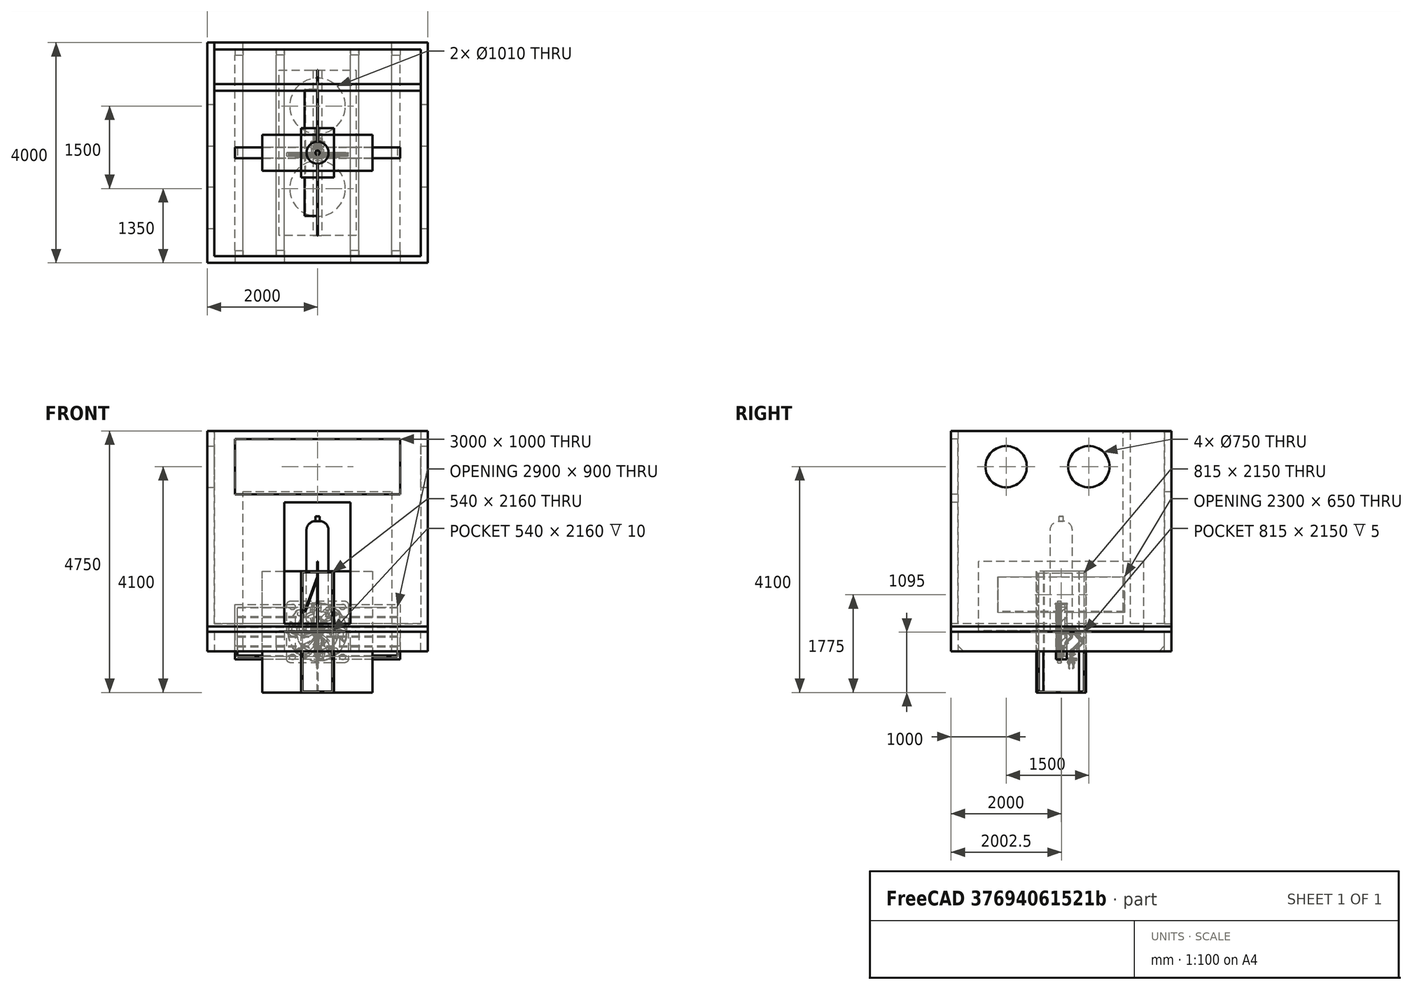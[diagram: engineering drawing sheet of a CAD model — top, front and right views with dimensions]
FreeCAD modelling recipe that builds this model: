
FCSTD DOCUMENT  (FreeCAD 0.19R22989 (Git))
Label: OCPMDC4_v2_asm
License: All rights reserved
LicenseURL: http://en.wikipedia.org/wiki/All_rights_reserved
objects: Part::Feature×54, App::Link×34, Sketcher::SketchObject×24, App::Part×19, TechDraw::DrawViewDimension×17, PartDesign::Pad×16, PartDesign::CoordinateSystem×13, PartDesign::Body×9, PartDesign::Pocket×6, TechDraw::DrawViewPart×6, Part::FeaturePython×3, App::MeasureDistance×3, TechDraw::DrawSVGTemplate×2, TechDraw::DrawPage×2, App::DocumentObjectGroup×2, PartDesign::Mirrored×2, PartDesign::Revolution×2, PartDesign::Chamfer×1, App::FeaturePython×1
note: 155 computed .brp shape members not serialized (recipe doc carries the construction recipe); baked Part::Feature solids carry a one-line shape summary decoded from their .brp

FEATURE [Sketcher::SketchObject] Sketch
  MapMode = 5
  Support = -> [XY_Plane]
  sketch-geometry (4):
    g0: LineSegment StartX=-1875 StartY=1875 StartZ=0 EndX=1875 EndY=1875 EndZ=0
    g1: LineSegment StartX=1875 StartY=1875 StartZ=0 EndX=1875 EndY=-1875 EndZ=0
    g2: LineSegment StartX=1875 StartY=-1875 StartZ=0 EndX=-1875 EndY=-1875 EndZ=0
    g3: LineSegment StartX=-1875 StartY=-1875 StartZ=0 EndX=-1875 EndY=1875 EndZ=0
  constraints (10):
    c: Coincident(g0,g1)
    c: Coincident(g1,g2)
    c: Coincident(g2,g3)
    c: Coincident(g3,g0)
    c: Horizontal(g2)
    c: Vertical(g3)
    c: DistanceX(g0,g0) = 3750
    c: DistanceY(g1,g1) = 3750
    c: Symmetric(g0,g0,g-2)
    c: Symmetric(g0,g1,g-1)
FEATURE [PartDesign::Pad] Pad
  Direction = (1,1,1)
  Length = 150
  Length2 = 100
  Profile = -> Sketch
  Type = 0
FEATURE [Sketcher::SketchObject] Sketch001
  ExternalGeometry = -> [Pad]
  MapMode = 5
  Placement = pos=(0,-1875,0) rot=(1,0,0;1.5708rad)
  Support = -> [Pad]
  sketch-geometry (16):
    g0: LineSegment StartX=-1350 StartY=0 StartZ=0 EndX=-1500 EndY=0 EndZ=0
    g1: LineSegment StartX=-1500 StartY=0 StartZ=0 EndX=-1500 EndY=-350 EndZ=0
    g2: LineSegment StartX=-1500 StartY=-350 StartZ=0 EndX=-1350 EndY=-350 EndZ=0
    g3: LineSegment StartX=-1350 StartY=-350 StartZ=0 EndX=-1350 EndY=0 EndZ=0
    g4: LineSegment StartX=-750 StartY=0 StartZ=0 EndX=-600 EndY=0 EndZ=0
    g5: LineSegment StartX=-600 StartY=0 StartZ=0 EndX=-600 EndY=-350 EndZ=0
    g6: LineSegment StartX=-600 StartY=-350 StartZ=0 EndX=-750 EndY=-350 EndZ=0
    g7: LineSegment StartX=-750 StartY=-350 StartZ=0 EndX=-750 EndY=0 EndZ=0
    g8: LineSegment StartX=600 StartY=0 StartZ=0 EndX=750 EndY=0 EndZ=0
    g9: LineSegment StartX=750 StartY=0 StartZ=0 EndX=750 EndY=-350 EndZ=0
    g10: LineSegment StartX=750 StartY=-350 StartZ=0 EndX=600 EndY=-350 EndZ=0
    g11: LineSegment StartX=600 StartY=-350 StartZ=0 EndX=600 EndY=0 EndZ=0
    g12: LineSegment StartX=1500 StartY=0 StartZ=0 EndX=1350 EndY=0 EndZ=0
    g13: LineSegment StartX=1350 StartY=0 StartZ=0 EndX=1350 EndY=-350 EndZ=0
    g14: LineSegment StartX=1350 StartY=-350 StartZ=0 EndX=1500 EndY=-350 EndZ=0
    g15: LineSegment StartX=1500 StartY=-350 StartZ=0 EndX=1500 EndY=0 EndZ=0
  constraints (48):
    c: Coincident(g0,g1)
    c: Coincident(g1,g2)
    c: Coincident(g2,g3)
    c: Coincident(g3,g0)
    c: Horizontal(g0)
    c: Horizontal(g2)
    c: Vertical(g1)
    c: Vertical(g3)
    c: PointOnObject(g0,g-1)
    c: DistanceX(g0,g0) = 150
    c: DistanceY(g2,g-1) = 350
    c: Coincident(g4,g5)
    c: Coincident(g5,g6)
    c: Coincident(g6,g7)
    c: Coincident(g7,g4)
    c: Horizontal(g4)
    c: Horizontal(g6)
    c: Vertical(g5)
    c: Vertical(g7)
    c: PointOnObject(g4,g-1)
    c: Coincident(g8,g9)
    c: Coincident(g9,g10)
    c: Coincident(g10,g11)
    c: Coincident(g11,g8)
    c: Horizontal(g8)
    c: Horizontal(g10)
    c: Vertical(g9)
    c: Vertical(g11)
    c: PointOnObject(g8,g-1)
    c: Coincident(g12,g13)
    c: Coincident(g13,g14)
    c: Coincident(g14,g15)
    c: Coincident(g15,g12)
    c: Horizontal(g12)
    c: Horizontal(g14)
    c: Vertical(g13)
    c: Vertical(g15)
    c: PointOnObject(g12,g-1)
    c: Horizontal(g6,g1)
    c: Horizontal(g1,g10)
    c: Horizontal(g10,g13)
    c: DistanceX(g4,g4) = 150
    c: DistanceX(g-3,g4) = 1275
    c: DistanceX(g-3,g0) = 375
    c: DistanceX(g12,g-4) = 375
    c: DistanceX(g12,g12) = 150
    c: DistanceX(g8,g-4) = 1275
    c: DistanceX(g8,g8) = 150
FEATURE [PartDesign::Pad] Pad001
  BaseFeature = -> Pad
  Direction = (1,1,1)
  Length = 3750
  Length2 = 100
  Profile = -> Sketch001
  Reversed = true
  Type = 0
FEATURE [PartDesign::Chamfer] Chamfer
  Angle = 45
  Base = -> Pad001 [Edge52,Edge58,Edge63,Edge67,Edge40,Edge34,Edge28,Edge22]
  BaseFeature = -> Pad001
  ChamferType = 0
  FlipDirection = false
  Size = 100
  Size2 = 1
  SupportTransform = false
FEATURE [Sketcher::SketchObject] Sketch002
  ExternalGeometry = -> [Chamfer]
  MapMode = 5
  Placement = pos=(-1875,0,0) rot=(0.57735,-0.57735,-0.57735;2.0944rad)
  Support = -> [Chamfer]
  sketch-geometry (4):
    g0: LineSegment StartX=-2000 StartY=-350 StartZ=0 EndX=2000 EndY=-350 EndZ=0
    g1: LineSegment StartX=2000 StartY=-350 StartZ=0 EndX=2000 EndY=3650 EndZ=0
    g2: LineSegment StartX=2000 StartY=3650 StartZ=0 EndX=-2000 EndY=3650 EndZ=0
    g3: LineSegment StartX=-2000 StartY=3650 StartZ=0 EndX=-2000 EndY=-350 EndZ=0
  constraints (12):
    c: Coincident(g0,g1)
    c: Coincident(g1,g2)
    c: Coincident(g2,g3)
    c: Coincident(g3,g0)
    c: Horizontal(g0)
    c: Horizontal(g2)
    c: Vertical(g1)
    c: Vertical(g3)
    c: DistanceX(g2,g2) = 4000
    c: DistanceY(g1,g1) = 4000
    c: DistanceX(g-1,g0) = 2000
    c: Horizontal(g0,g-5)
FEATURE [PartDesign::Pad] Pad002
  BaseFeature = -> Chamfer
  Direction = (1,1,1)
  Length = 125
  Length2 = 100
  Profile = -> Sketch002
  Type = 0
FEATURE [Sketcher::SketchObject] Sketch003
  ExternalGeometry = -> [Pad002]
  MapMode = 5
  Placement = pos=(1875,0,0) rot=(0.57735,0.57735,0.57735;2.0944rad)
  Support = -> [Pad002]
  sketch-geometry (4):
    g0: LineSegment StartX=1250 StartY=150 StartZ=0 EndX=1125 EndY=150 EndZ=0
    g1: LineSegment StartX=1125 StartY=150 StartZ=0 EndX=1125 EndY=3637.44 EndZ=0
    g2: LineSegment StartX=1125 StartY=3637.44 StartZ=0 EndX=1250 EndY=3637.44 EndZ=0
    g3: LineSegment StartX=1250 StartY=3637.44 StartZ=0 EndX=1250 EndY=150 EndZ=0
  constraints (12):
    c: Coincident(g0,g1)
    c: Coincident(g1,g2)
    c: Coincident(g2,g3)
    c: Coincident(g3,g0)
    c: Horizontal(g0)
    c: Horizontal(g2)
    c: Vertical(g1)
    c: Vertical(g3)
    c: PointOnObject(g0,g-7)
    c: DistanceX(g2,g2) = 125
    c: DistanceX(g-7,g1) = 3000
    c: DistanceY(g3,g3) = 3487.44
FEATURE [PartDesign::Pad] Pad003
  BaseFeature = -> Pad002
  Direction = (1,1,1)
  Length = 3750
  Length2 = 100
  Profile = -> Sketch003
  Reversed = true
  Type = 0
FEATURE [Sketcher::SketchObject] Sketch004
  ExternalGeometry = -> [Pad003]
  MapMode = 5
  Placement = pos=(1875,0,0) rot=(0.57735,0.57735,0.57735;2.0944rad)
  Support = -> [Pad003]
  sketch-geometry (4):
    g0: LineSegment StartX=-2000 StartY=3650 StartZ=0 EndX=2000 EndY=3650 EndZ=0
    g1: LineSegment StartX=2000 StartY=3650 StartZ=0 EndX=2000 EndY=-350 EndZ=0
    g2: LineSegment StartX=2000 StartY=-350 StartZ=0 EndX=-2000 EndY=-350 EndZ=0
    g3: LineSegment StartX=-2000 StartY=-350 StartZ=0 EndX=-2000 EndY=3650 EndZ=0
  constraints (10):
    c: Coincident(g0,g1)
    c: Coincident(g1,g2)
    c: Coincident(g2,g3)
    c: Coincident(g3,g0)
    c: Horizontal(g0)
    c: Horizontal(g2)
    c: Vertical(g1)
    c: Vertical(g3)
    c: Coincident(g0,g-4)
    c: Coincident(g1,g-5)
FEATURE [PartDesign::Pad] Pad004
  BaseFeature = -> Pad003
  Direction = (1,1,1)
  Length = 125
  Length2 = 100
  Profile = -> Sketch004
  Type = 0
FEATURE [Sketcher::SketchObject] Sketch005
  ExternalGeometry = -> [Pad004]
  MapMode = 5
  Placement = pos=(0,-1875,0) rot=(1,0,0;1.5708rad)
  Support = -> [Pad004]
  sketch-geometry (12):
    g0: LineSegment StartX=-1875 StartY=3650 StartZ=0 EndX=1875 EndY=3650 EndZ=0
    g1: LineSegment StartX=1875 StartY=3650 StartZ=0 EndX=1875 EndY=-350 EndZ=0
    g2: LineSegment StartX=1875 StartY=-350 StartZ=0 EndX=-1875 EndY=-350 EndZ=0
    g3: LineSegment StartX=-1875 StartY=-350 StartZ=0 EndX=-1875 EndY=3650 EndZ=0
    g4: LineSegment StartX=-600 StartY=150 StartZ=0 EndX=600 EndY=150 EndZ=0
    g5: LineSegment StartX=600 StartY=150 StartZ=0 EndX=600 EndY=2350 EndZ=0
    g6: LineSegment StartX=600 StartY=2350 StartZ=0 EndX=-600 EndY=2350 EndZ=0
    g7: LineSegment StartX=-600 StartY=2350 StartZ=0 EndX=-600 EndY=150 EndZ=0
    g8: LineSegment StartX=-1500 StartY=3500 StartZ=0 EndX=1500 EndY=3500 EndZ=0
    g9: LineSegment StartX=1500 StartY=3500 StartZ=0 EndX=1500 EndY=2500 EndZ=0
    g10: LineSegment StartX=1500 StartY=2500 StartZ=0 EndX=-1500 EndY=2500 EndZ=0
    g11: LineSegment StartX=-1500 StartY=2500 StartZ=0 EndX=-1500 EndY=3500 EndZ=0
  constraints (33):
    c: Coincident(g0,g1)
    c: Coincident(g1,g2)
    c: Coincident(g2,g3)
    c: Coincident(g3,g0)
    c: Horizontal(g0)
    c: Horizontal(g2)
    c: Vertical(g1)
    c: Vertical(g3)
    c: Coincident(g0,g-4)
    c: Coincident(g1,g-6)
    c: Coincident(g4,g5)
    c: Coincident(g5,g6)
    c: Coincident(g6,g7)
    c: Coincident(g7,g4)
    c: Horizontal(g4)
    c: Horizontal(g6)
    c: Vertical(g5)
    c: Vertical(g7)
    c: PointOnObject(g4,g-7)
    c: DistanceX(g6,g6) = 1200
    c: DistanceY(g-1,g5) = 2350
    c: DistanceX(g-1,g4) = 600
    c: Coincident(g8,g9)
    c: Coincident(g9,g10)
    c: Coincident(g10,g11)
    c: Coincident(g11,g8)
    c: Horizontal(g10)
    c: Vertical(g9)
    c: Vertical(g11)
    c: Symmetric(g8,g8,g-2)
    c: DistanceY(g-1,g9) = 2500
    c: DistanceY(g9,g9) = 1000
    c: DistanceX(g8,g8) = 3000
FEATURE [PartDesign::Pad] Pad005
  BaseFeature = -> Pad004
  Direction = (1,1,1)
  Length = 125
  Length2 = 100
  Profile = -> Sketch005
  Type = 0
FEATURE [Sketcher::SketchObject] Sketch006
  ExternalGeometry = -> [Pad005]
  MapMode = 5
  Placement = pos=(0,1875,0) rot=(0,0.707107,0.707107;3.14159rad)
  Support = -> [Pad005]
  sketch-geometry (8):
    g0: LineSegment StartX=-1875 StartY=3650 StartZ=0 EndX=1875 EndY=3637.44 EndZ=0
    g1: LineSegment StartX=1875 StartY=-350 StartZ=0 EndX=-1875 EndY=-350 EndZ=0
    g2: LineSegment StartX=-1875 StartY=-350 StartZ=0 EndX=-1875 EndY=3650 EndZ=0
    g3: LineSegment StartX=-1350 StartY=150 StartZ=0 EndX=1350 EndY=150 EndZ=0
    g4: LineSegment StartX=1350 StartY=150 StartZ=0 EndX=1350 EndY=2550 EndZ=0
    g5: LineSegment StartX=1350 StartY=2550 StartZ=0 EndX=-1350 EndY=2550 EndZ=0
    g6: LineSegment StartX=-1350 StartY=2550 StartZ=0 EndX=-1350 EndY=150 EndZ=0
    g7: LineSegment StartX=1875 StartY=3637.44 StartZ=0 EndX=1875 EndY=-350 EndZ=0
  constraints (20):
    c: Coincident(g1,g2)
    c: Coincident(g2,g0)
    c: Vertical(g2)
    c: Coincident(g3,g4)
    c: Coincident(g4,g5)
    c: Coincident(g5,g6)
    c: Coincident(g6,g3)
    c: Horizontal(g3)
    c: Horizontal(g5)
    c: Vertical(g4)
    c: Vertical(g6)
    c: PointOnObject(g3,g-5)
    c: DistanceX(g5,g-1) = 1350
    c: DistanceX(g-1,g4) = 1350
    c: DistanceY(g-1,g4) = 2550
    c: Coincident(g-6,g1)
    c: Coincident(g0,g-7)
    c: Coincident(g7,g0)
    c: Coincident(g7,g1)
    c: Coincident(g1,g-4)
FEATURE [PartDesign::Pad] Pad006
  BaseFeature = -> Pad005
  Direction = (1,1,1)
  Length = 125
  Length2 = 100
  Profile = -> Sketch006
  Type = 0
FEATURE [Sketcher::SketchObject] Sketch008
  MapMode = 5
  Placement = pos=(0,1850,-1.054e-12) rot=(0,0.707107,0.707107;3.14159rad)
  sketch-geometry (4):
    g0: LineSegment StartX=385.941 StartY=1661.56 StartZ=0 EndX=683.703 EndY=1661.56 EndZ=0
    g1: LineSegment StartX=683.703 StartY=1661.56 StartZ=0 EndX=683.703 EndY=1503.07 EndZ=0
    g2: LineSegment StartX=683.703 StartY=1503.07 StartZ=0 EndX=385.941 EndY=1503.07 EndZ=0
    g3: LineSegment StartX=385.941 StartY=1503.07 StartZ=0 EndX=385.941 EndY=1661.56 EndZ=0
  constraints (8):
    c: Coincident(g0,g1)
    c: Coincident(g1,g2)
    c: Coincident(g2,g3)
    c: Coincident(g3,g0)
    c: Horizontal(g0)
    c: Horizontal(g2)
    c: Vertical(g1)
    c: Vertical(g3)
FEATURE [PartDesign::Pocket] Pocket
  BaseFeature = -> Pad006
  Length = 5
  Length2 = 100
  Profile = -> Sketch008
  Type = 0
FEATURE [TechDraw::DrawSVGTemplate] Template
  EditableTexts = AUTHOR_NAME=AUTHOR NAME; DN=DN; DRAWING_TITLE=DRAWING TITLE; FC-DATE=DD/MM/YYYY; FC-REV=REV A; FC-SC=SCALE; FC-SH=1 / 3; FC-SI=A3; FreeCAD_DRAWING=FreeCAD DRAWING; PN=PN
  Height = 297
  Orientation = 1
  Width = 420
FEATURE [TechDraw::DrawSVGTemplate] Template001
  EditableTexts = AUTHOR_NAME=Karl Rabe; DN=DN; DRAWING_TITLE=DRAWING TITLE; FC-DATE=DD/MM/YYYY; FC-REV=REV A; FC-SC=SCALE; FC-SH=2 / 3; FC-SI=A3; FreeCAD_DRAWING=FreeCAD DRAWING; PN=PN
  Height = 297
  Orientation = 1
  Width = 420
FEATURE [Sketcher::SketchObject] Sketch009
  ExternalGeometry = -> [Pad006]
  MapMode = 5
  Placement = pos=(2000,0,0) rot=(0.57735,0.57735,0.57735;2.0944rad)
  Support = -> [Pad006]
  sketch-geometry (2):
    g0: Circle CenterX=-1000 CenterY=3000 CenterZ=0 NormalX=0 NormalY=0 NormalZ=1 AngleXU=0 Radius=375
    g1: Circle CenterX=500 CenterY=3000 CenterZ=0 NormalX=0 NormalY=0 NormalZ=1 AngleXU=0 Radius=375
  constraints (6):
    c: Horizontal(g1,g0)
    c: Equal(g1,g0)
    c: Radius(g1) = 375
    c: DistanceX(g0,g1) = 1500
    c: DistanceX(g1,g-4) = 1500
    c: DistanceY(g-1,g1) = 3000
FEATURE [PartDesign::Pocket] Pocket001
  BaseFeature = -> Pocket
  Length = 5
  Length2 = 100
  Profile = -> Sketch009
  Type = 1
FEATURE [PartDesign::Body] Body
  Group = -> [Sketch,Pad,Sketch001,Pad001,Chamfer,Sketch002,Pad002,Sketch003,Pad003,Sketch004,Pad004,Sketch005,Pad005,Sketch006,Pad006,Sketch008,Pocket,Sketch009,Pocket001]
  Origin = -> Origin
  Tip = -> Pocket001
FEATURE [TechDraw::DrawViewPart] View
  CoarseView = false
  Direction = (0,1,0)
  Focus = 100
  HardHidden = false
  IsoCount = 0
  IsoHidden = false
  IsoVisible = false
  LockPosition = false
  Perspective = false
  Rotation = 0
  Scale = 0.03
  ScaleType = 0
  SeamHidden = false
  SeamVisible = true
  SmoothHidden = false
  SmoothVisible = true
  Source = -> [Body]
  X = 91.7881
  XDirection = (-1,0,0)
  Y = 79.6901
FEATURE [TechDraw::DrawViewPart] View001
  CoarseView = false
  Direction = (0.577,-0.577,0.577)
  Focus = 100
  HardHidden = false
  IsoCount = 0
  IsoHidden = false
  IsoVisible = false
  LockPosition = false
  Perspective = false
  Rotation = 0
  Scale = 0.03
  ScaleType = 0
  SeamHidden = false
  SeamVisible = true
  SmoothHidden = false
  SmoothVisible = true
  Source = -> [Body]
  X = 319.007
  XDirection = (0.707,0.707,0)
  Y = 180.197
FEATURE [TechDraw::DrawViewPart] View002
  CoarseView = false
  Direction = (0,-1,0)
  Focus = 100
  HardHidden = false
  IsoCount = 0
  IsoHidden = false
  IsoVisible = false
  LockPosition = false
  Perspective = false
  Rotation = 0
  Scale = 0.03
  ScaleType = 0
  SeamHidden = false
  SeamVisible = true
  SmoothHidden = false
  SmoothVisible = true
  Source = -> [Body]
  X = 85.5454
  XDirection = (1,0,0)
  Y = 223.432
FEATURE [TechDraw::DrawViewDimension] Dimension
  Arbitrary = false
  FormatSpec = %.2f
  Inverted = false
  LockPosition = false
  MeasureType = 1
  OverTolerance = 0
  References2D = -> [View002]
  Rotation = 0
  ScaleType = 0
  TheoreticalExact = false
  Type = 1
  UnderTolerance = 0
  X = 99.6805
  Y = -47.3302
FEATURE [TechDraw::DrawViewDimension] Dimension001
  Arbitrary = false
  FormatSpec = %.2f
  Inverted = false
  LockPosition = false
  MeasureType = 1
  OverTolerance = 0
  References2D = -> [View002]
  Rotation = 0
  ScaleType = 0
  TheoreticalExact = false
  Type = 2
  UnderTolerance = 0
  X = 69.5232
  Y = -10.7054
FEATURE [TechDraw::DrawViewDimension] Dimension002
  Arbitrary = false
  FormatSpec = %.2f
  Inverted = false
  LockPosition = false
  MeasureType = 1
  OverTolerance = 0
  References2D = -> [View002]
  Rotation = 0
  ScaleType = 0
  TheoreticalExact = false
  Type = 2
  UnderTolerance = 0
  X = 117.416
  Y = -4.47397
FEATURE [TechDraw::DrawViewDimension] Dimension003
  Arbitrary = false
  FormatSpec = %.2f
  Inverted = false
  LockPosition = false
  MeasureType = 1
  OverTolerance = 0
  References2D = -> [View002]
  Rotation = 0
  ScaleType = 0
  TheoreticalExact = false
  Type = 1
  UnderTolerance = 0
  X = -1.26083
  Y = -71.0968
FEATURE [TechDraw::DrawViewDimension] Dimension004
  Arbitrary = false
  FormatSpec = %.2f
  Inverted = false
  LockPosition = false
  MeasureType = 1
  OverTolerance = 0
  References2D = -> [View]
  Rotation = 0
  ScaleType = 0
  TheoreticalExact = false
  Type = 2
  UnderTolerance = 0
  X = 92.6963
  Y = -9.93208
FEATURE [TechDraw::DrawViewDimension] Dimension005
  Arbitrary = false
  FormatSpec = %.2f
  Inverted = false
  LockPosition = false
  MeasureType = 1
  OverTolerance = 0
  References2D = -> [View]
  Rotation = 0
  ScaleType = 0
  TheoreticalExact = false
  Type = 1
  UnderTolerance = 0
  X = 0.621385
  Y = 41.6025
FEATURE [TechDraw::DrawViewDimension] Dimension006
  Arbitrary = false
  FormatSpec = %.2f
  Inverted = false
  LockPosition = false
  MeasureType = 1
  OverTolerance = 0
  References2D = -> [View]
  Rotation = 0
  ScaleType = 0
  TheoreticalExact = false
  Type = 1
  UnderTolerance = 0
  X = 93.1051
  Y = 62.3635
FEATURE [TechDraw::DrawPage] Page
  KeepUpdated = true
  NextBalloonIndex = 1
  ProjectionType = 0
  Template = -> Template
  Views = -> [View,View001,View002,Dimension,Dimension001,Dimension002,Dimension003,Dimension004,Dimension005,Dimension006]
FEATURE [TechDraw::DrawViewPart] View003  label="Bottom View"
  CoarseView = false
  Direction = (0,0,-1)
  Focus = 100
  HardHidden = false
  IsoCount = 0
  IsoHidden = false
  IsoVisible = false
  LockPosition = false
  Perspective = false
  Rotation = 0
  Scale = 0.03
  ScaleType = 0
  SeamHidden = false
  SeamVisible = true
  SmoothHidden = false
  SmoothVisible = true
  Source = -> [Body]
  X = 85.4042
  XDirection = (1,0,0)
  Y = 73.347
FEATURE [TechDraw::DrawViewPart] View004  label="Top View"
  CoarseView = false
  Direction = (0,0,1)
  Focus = 100
  HardHidden = false
  IsoCount = 0
  IsoHidden = false
  IsoVisible = false
  LockPosition = false
  Perspective = false
  Rotation = 0
  Scale = 0.03
  ScaleType = 0
  SeamHidden = false
  SeamVisible = true
  SmoothHidden = false
  SmoothVisible = true
  Source = -> [Body]
  X = 341.518
  XDirection = (1,0,0)
  Y = 192.998
FEATURE [TechDraw::DrawViewPart] View005  label="Site View"
  CoarseView = false
  Direction = (-1,0,0)
  Focus = 100
  HardHidden = false
  IsoCount = 0
  IsoHidden = false
  IsoVisible = false
  LockPosition = false
  Perspective = false
  Rotation = 0
  Scale = 0.03
  ScaleType = 0
  SeamHidden = false
  SeamVisible = true
  SmoothHidden = false
  SmoothVisible = true
  Source = -> [Body]
  X = 90.8429
  XDirection = (0,-1,0)
  Y = 221.675
FEATURE [TechDraw::DrawViewDimension] Dimension007
  Arbitrary = false
  FormatSpec = %.2f
  Inverted = false
  LockPosition = false
  MeasureType = 1
  OverTolerance = 0
  References2D = -> [View005]
  Rotation = 0
  Scale = 0.03
  ScaleType = 0
  TheoreticalExact = false
  Type = 2
  UnderTolerance = 0
  X = 83.9215
  Y = -2.70809
FEATURE [TechDraw::DrawViewDimension] Dimension008
  Arbitrary = false
  FormatSpec = %.2f
  Inverted = false
  LockPosition = false
  MeasureType = 1
  OverTolerance = 0
  References2D = -> [View005]
  Rotation = 0
  Scale = 0.03
  ScaleType = 0
  TheoreticalExact = false
  Type = 1
  UnderTolerance = 0
  X = 0
  Y = 43.1071
FEATURE [TechDraw::DrawViewDimension] Dimension009
  Arbitrary = false
  FormatSpec = %.2f
  Inverted = false
  LockPosition = false
  MeasureType = 1
  OverTolerance = 0
  References2D = -> [View004]
  Rotation = 0
  Scale = 0.03
  ScaleType = 0
  TheoreticalExact = false
  Type = 2
  UnderTolerance = 0
  X = 45.1254
  Y = -11.662
FEATURE [TechDraw::DrawViewDimension] Dimension010
  Arbitrary = false
  FormatSpec = %.2f
  Inverted = false
  LockPosition = false
  MeasureType = 1
  OverTolerance = 0
  References2D = -> [View004]
  Rotation = 0
  Scale = 0.03
  ScaleType = 0
  TheoreticalExact = false
  Type = 1
  UnderTolerance = 0
  X = 3.29618
  Y = -41.8292
FEATURE [TechDraw::DrawViewDimension] Dimension011
  Arbitrary = false
  FormatSpec = %.2f
  Inverted = false
  LockPosition = false
  MeasureType = 1
  OverTolerance = 0
  References2D = -> [View004]
  Rotation = 0
  Scale = 0.03
  ScaleType = 0
  TheoreticalExact = false
  Type = 2
  UnderTolerance = 0
  X = -83.8555
  Y = 48.5231
FEATURE [TechDraw::DrawViewDimension] Dimension012
  Arbitrary = false
  FormatSpec = %.2f
  Inverted = false
  LockPosition = false
  MeasureType = 1
  OverTolerance = 0
  References2D = -> [View003]
  Rotation = 0
  Scale = 0.03
  ScaleType = 0
  TheoreticalExact = false
  Type = 1
  UnderTolerance = 0
  X = 83.626
  Y = 41.3648
FEATURE [TechDraw::DrawViewDimension] Dimension013
  Arbitrary = false
  FormatSpec = %.2f
  Inverted = false
  LockPosition = false
  MeasureType = 1
  OverTolerance = 0
  References2D = -> [View003]
  Rotation = 0
  Scale = 0.03
  ScaleType = 0
  TheoreticalExact = false
  Type = 1
  UnderTolerance = 0
  X = 86.0275
  Y = 21.9967
FEATURE [TechDraw::DrawViewDimension] Dimension014
  Arbitrary = false
  FormatSpec = %.2f
  Inverted = false
  LockPosition = false
  MeasureType = 1
  OverTolerance = 0
  References2D = -> [View003]
  Rotation = 0
  Scale = 0.03
  ScaleType = 0
  TheoreticalExact = false
  Type = 1
  UnderTolerance = 0
  X = 82.7558
  Y = 3.28396
FEATURE [TechDraw::DrawViewDimension] Dimension015
  Arbitrary = false
  FormatSpec = %.2f
  Inverted = false
  LockPosition = false
  MeasureType = 1
  OverTolerance = 0
  References2D = -> [View003]
  Rotation = 0
  Scale = 0.03
  ScaleType = 0
  TheoreticalExact = false
  Type = 1
  UnderTolerance = 0
  X = 85.0968
  Y = -12.9299
FEATURE [TechDraw::DrawViewDimension] Dimension016
  Arbitrary = false
  FormatSpec = %.2f
  Inverted = false
  LockPosition = false
  MeasureType = 1
  OverTolerance = 0
  References2D = -> [View003]
  Rotation = 0
  Scale = 0.03
  ScaleType = 0
  TheoreticalExact = false
  Type = 1
  UnderTolerance = 0
  X = 87.0997
  Y = 72.9408
FEATURE [TechDraw::DrawPage] Page001
  KeepUpdated = true
  NextBalloonIndex = 1
  ProjectionType = 0
  Scale = 0.03
  Template = -> Template001
  Views = -> [View003,View004,View005,Dimension007,Dimension008,Dimension009,Dimension010,Dimension011,Dimension012,Dimension013,Dimension014,Dimension015,Dimension016]
FEATURE [PartDesign::CoordinateSystem] LCS_Origin
  AttacherType = Attacher::AttachEngine3D
  MapMode = 2
  Support = -> [X_Axis001]
FEATURE [App::DocumentObjectGroup] Constraints
FEATURE [App::FeaturePython] Variables  # WARN: FeaturePython — macro-defined, semantics opaque (R4)
FEATURE [PartDesign::CoordinateSystem] LCS_0
  AttacherType = Attacher::AttachEngine3D
  MapMode = 2
  Support = -> [X_Axis002]
FEATURE [App::Part] OCPMDC4mv2
  Group = -> [LCS_0,Body]
  Origin = -> Origin002
FEATURE [PartDesign::CoordinateSystem] LCS_0002
  AttacherType = Attacher::AttachEngine3D
  MapMode = 2
  Support = -> [X_Axis004]
FEATURE [PartDesign::CoordinateSystem] LCS_0003
  AttacherType = Attacher::AttachEngine3D
  MapMode = 2
  Support = -> [X_Axis005]
FEATURE [PartDesign::CoordinateSystem] LCS_0004
  AttacherType = Attacher::AttachEngine3D
  MapMode = 2
  Support = -> [X_Axis006]
FEATURE [PartDesign::CoordinateSystem] LCS_0005
  AttacherType = Attacher::AttachEngine3D
  MapMode = 2
  Support = -> [X_Axis007]
FEATURE [PartDesign::CoordinateSystem] LCS_0006
  AttacherType = Attacher::AttachEngine3D
  MapMode = 2
  Support = -> [X_Axis008]
FEATURE [Sketcher::SketchObject] Sketch012
  MapMode = 5
  Placement = pos=(0,0,0) rot=(1,0,0;1.5708rad)
  Support = -> [XZ_Plane009]
  sketch-geometry (4):
    g0: LineSegment StartX=-300 StartY=1100 StartZ=0 EndX=300 EndY=1100 EndZ=0
    g1: LineSegment StartX=300 StartY=1100 StartZ=0 EndX=300 EndY=-1100 EndZ=0
    g2: LineSegment StartX=300 StartY=-1100 StartZ=0 EndX=-300 EndY=-1100 EndZ=0
    g3: LineSegment StartX=-300 StartY=-1100 StartZ=0 EndX=-300 EndY=1100 EndZ=0
  constraints (12):
    c: Coincident(g0,g1)
    c: Coincident(g1,g2)
    c: Coincident(g2,g3)
    c: Coincident(g3,g0)
    c: Horizontal(g0)
    c: Horizontal(g2)
    c: Vertical(g1)
    c: Vertical(g3)
    c: DistanceX(g-1,g0) = 300
    c: DistanceX(g0,g0) = 600
    c: DistanceY(g1,g1) = 2200
    c: DistanceY(g-1,g0) = 1100
FEATURE [PartDesign::Pad] Pad007
  Direction = (1,1,1)
  Length = 900
  Length2 = 100
  Midplane = true
  Placement = pos=(0,0,0) rot=(1,0,0;1.5708rad)
  Profile = -> Sketch012
  Type = 0
FEATURE [Sketcher::SketchObject] Sketch010
  ExternalGeometry = -> [Pad007]
  MapMode = 5
  Placement = pos=(0,-450,9.9e-14) rot=(1,0,0;1.5708rad)
  Support = -> [Pad007]
  sketch-geometry (4):
    g0: LineSegment StartX=-270 StartY=1080 StartZ=0 EndX=270 EndY=1080 EndZ=0
    g1: LineSegment StartX=270 StartY=1080 StartZ=0 EndX=270 EndY=-1080 EndZ=0
    g2: LineSegment StartX=270 StartY=-1080 StartZ=0 EndX=-270 EndY=-1080 EndZ=0
    g3: LineSegment StartX=-270 StartY=-1080 StartZ=0 EndX=-270 EndY=1080 EndZ=0
  constraints (12):
    c: Coincident(g0,g1)
    c: Coincident(g1,g2)
    c: Coincident(g2,g3)
    c: Coincident(g3,g0)
    c: Horizontal(g0)
    c: Horizontal(g2)
    c: Vertical(g1)
    c: Vertical(g3)
    c: DistanceY(g0,g-3) = 20
    c: DistanceX(g0,g-3) = 30
    c: DistanceY(g-6,g1) = 20
    c: DistanceX(g-5,g2) = 30
FEATURE [PartDesign::Pocket] Pocket002
  BaseFeature = -> Pad007
  Length = 10
  Length2 = 100
  Placement = pos=(0,0,0) rot=(1,0,0;1.5708rad)
  Profile = -> Sketch010
  Type = 0
FEATURE [PartDesign::Mirrored] Mirrored
  BaseFeature = -> Pocket002
  MirrorPlane = -> XZ_Plane009
  Originals = -> [Pocket002]
  Placement = pos=(0,0,0) rot=(1,0,0;1.5708rad)
FEATURE [Sketcher::SketchObject] Sketch011
  ExternalGeometry = -> [Mirrored]
  MapMode = 5
  Placement = pos=(300,0,0) rot=(0.707107,0,0.707107;3.14159rad)
  Support = -> [Mirrored]
  sketch-geometry (4):
    g0: LineSegment StartX=-1080 StartY=405 StartZ=0 EndX=1070 EndY=405 EndZ=0
    g1: LineSegment StartX=1070 StartY=405 StartZ=0 EndX=1070 EndY=-410 EndZ=0
    g2: LineSegment StartX=1070 StartY=-410 StartZ=0 EndX=-1080 EndY=-410 EndZ=0
    g3: LineSegment StartX=-1080 StartY=-410 StartZ=0 EndX=-1080 EndY=405 EndZ=0
  constraints (12):
    c: Coincident(g0,g1)
    c: Coincident(g1,g2)
    c: Coincident(g2,g3)
    c: Coincident(g3,g0)
    c: Horizontal(g0)
    c: Horizontal(g2)
    c: Vertical(g1)
    c: Vertical(g3)
    c: DistanceX(g-4,g2) = 20
    c: DistanceY(g-4,g2) = 40
    c: DistanceX(g0,g-6) = 30
    c: DistanceY(g0,g-6) = 45
FEATURE [PartDesign::Pocket] Pocket003
  BaseFeature = -> Mirrored
  Length = 5
  Length2 = 100
  Placement = pos=(0,0,0) rot=(1,0,0;1.5708rad)
  Profile = -> Sketch011
  Type = 0
FEATURE [PartDesign::Mirrored] Mirrored001
  BaseFeature = -> Pocket003
  MirrorPlane = -> YZ_Plane009
  Originals = -> [Pocket003]
  Placement = pos=(0,0,0) rot=(1,0,0;1.5708rad)
FEATURE [PartDesign::Body] Body001
  Group = -> [Sketch012,Pad007,Sketch010,Pocket002,Mirrored,Sketch011,Pocket003,Mirrored001]
  Origin = -> Origin009
  Tip = -> Mirrored001
FEATURE [App::Part] Part  label="OCPRack001"
  Group = -> [LCS_0006,Body001]
  Origin = -> Origin008
FEATURE [Sketcher::SketchObject] Sketch013
  MapMode = 5
  Support = -> [XY_Plane010]
  sketch-geometry (4):
    g0: LineSegment StartX=-2000 StartY=2000 StartZ=0 EndX=2000 EndY=2000 EndZ=0
    g1: LineSegment StartX=2000 StartY=2000 StartZ=0 EndX=2000 EndY=-2000 EndZ=0
    g2: LineSegment StartX=2000 StartY=-2000 StartZ=0 EndX=-2000 EndY=-2000 EndZ=0
    g3: LineSegment StartX=-2000 StartY=-2000 StartZ=0 EndX=-2000 EndY=2000 EndZ=0
  constraints (10):
    c: Coincident(g0,g1)
    c: Coincident(g1,g2)
    c: Coincident(g2,g3)
    c: Coincident(g3,g0)
    c: Horizontal(g2)
    c: Vertical(g3)
    c: DistanceX(g0,g0) = 4000
    c: DistanceY(g3,g3) = 4000
    c: Symmetric(g0,g0,g-2)
    c: Symmetric(g0,g1,g-1)
FEATURE [PartDesign::Pad] Pad008
  Direction = (1,1,1)
  Length = 100
  Length2 = 100
  Profile = -> Sketch013
  Type = 0
FEATURE [PartDesign::Body] Body002
  Group = -> [Sketch013,Pad008]
  Origin = -> Origin010
  Tip = -> Pad008
FEATURE [App::Part] Roof
  Group = -> [LCS_0003,Body002]
  Origin = -> Origin005
FEATURE [Sketcher::SketchObject] Sketch014
  MapMode = 5
  Placement = pos=(0,0,0) rot=(1,0,0;1.5708rad)
  Support = -> [XZ_Plane011]
  sketch-geometry (6):
    g0: LineSegment StartX=200 StartY=0 StartZ=0 EndX=200 EndY=1850 EndZ=0
    g1: LineSegment StartX=40 StartY=2010 StartZ=0 EndX=40 EndY=2100 EndZ=0
    g2: LineSegment StartX=200 StartY=0 StartZ=0 EndX=0 EndY=0 EndZ=0
    g3: LineSegment StartX=40 StartY=2100 StartZ=0 EndX=0 EndY=2100 EndZ=0
    g4: LineSegment StartX=0 StartY=2100 StartZ=0 EndX=0 EndY=0 EndZ=0
    g5: ArcOfCircle CenterX=40 CenterY=1850 CenterZ=0 NormalX=0 NormalY=0 NormalZ=1 AngleXU=0 Radius=160 StartAngle=0 EndAngle=1.5708
  constraints (17):
    c: Vertical(g0)
    c: Vertical(g1)
    c: Horizontal(g2)
    c: Vertical(g4)
    c: Coincident(g5,g1)
    c: Horizontal(g3)
    c: Coincident(g3,g1)
    c: Tangent(g5,g0) = -1.5708
    c: Coincident(g0,g2)
    c: Coincident(g2,g4)
    c: Coincident(g2,g-1)
    c: DistanceX(g2,g2) = 200
    c: Perpendicular(g5,g1)
    c: Coincident(g4,g3)
    c: DistanceY(g2,g3) = 2100
    c: DistanceY(g1,g1) = 90
    c: DistanceX(g3,g1) = 40
FEATURE [PartDesign::Revolution] Revolution
  Angle = 360
  Axis = (0,2e-16,1)
  Base = (0,0,0)
  Placement = pos=(0,0,0) rot=(1,0,0;1.5708rad)
  Profile = -> Sketch014
  ReferenceAxis = -> Sketch014 [V_Axis]
  Reversed = true
FEATURE [PartDesign::Body] Body003
  Group = -> [Sketch014,Revolution]
  Origin = -> Origin011
  Tip = -> Revolution
FEATURE [App::Part] Loeschflasche
  Group = -> [LCS_0005,Body003]
  Origin = -> Origin007
FEATURE [Sketcher::SketchObject] Sketch016
  MapMode = 5
  Placement = pos=(0,0,0) rot=(1,0,0;1.5708rad)
  Support = -> [XZ_Plane012]
  sketch-geometry (4):
    g0: LineSegment StartX=-1000 StartY=1100 StartZ=0 EndX=1000 EndY=1100 EndZ=0
    g1: LineSegment StartX=1000 StartY=1100 StartZ=0 EndX=1000 EndY=-1100 EndZ=0
    g2: LineSegment StartX=1000 StartY=-1100 StartZ=0 EndX=-1000 EndY=-1100 EndZ=0
    g3: LineSegment StartX=-1000 StartY=-1100 StartZ=0 EndX=-1000 EndY=1100 EndZ=0
  constraints (12):
    c: Coincident(g0,g1)
    c: Coincident(g1,g2)
    c: Coincident(g2,g3)
    c: Coincident(g3,g0)
    c: Horizontal(g0)
    c: Horizontal(g2)
    c: Vertical(g1)
    c: Vertical(g3)
    c: DistanceX(g0,g0) = 2000
    c: DistanceY(g1,g1) = 2200
    c: DistanceY(g-1,g0) = 1100
    c: DistanceX(g-1,g1) = 1000
FEATURE [PartDesign::Pad] Pad009
  Direction = (1,1,1)
  Length = 650
  Length2 = 100
  Midplane = true
  Placement = pos=(0,0,0) rot=(1,0,0;1.5708rad)
  Profile = -> Sketch016
  Type = 0
FEATURE [Sketcher::SketchObject] Sketch015
  ExternalGeometry = -> [Pad009]
  MapMode = 5
  Placement = pos=(0,-325,7.15e-14) rot=(1,0,0;1.5708rad)
  Support = -> [Pad009]
  sketch-geometry (4):
    g0: LineSegment StartX=-5 StartY=1100 StartZ=0 EndX=5 EndY=1100 EndZ=0
    g1: LineSegment StartX=5 StartY=1100 StartZ=0 EndX=5 EndY=-1100 EndZ=0
    g2: LineSegment StartX=5 StartY=-1100 StartZ=0 EndX=-5 EndY=-1100 EndZ=0
    g3: LineSegment StartX=-5 StartY=-1100 StartZ=0 EndX=-5 EndY=1100 EndZ=0
  constraints (11):
    c: Coincident(g0,g1)
    c: Coincident(g1,g2)
    c: Coincident(g2,g3)
    c: Coincident(g3,g0)
    c: Horizontal(g2)
    c: Vertical(g1)
    c: Vertical(g3)
    c: Horizontal(g0,g-3)
    c: DistanceX(g0,g0) = 10
    c: Symmetric(g0,g0,g-2)
    c: Horizontal(g1,g-4)
FEATURE [PartDesign::Pocket] Pocket004
  BaseFeature = -> Pad009
  Length = 10
  Length2 = 100
  Placement = pos=(0,0,0) rot=(1,0,0;1.5708rad)
  Profile = -> Sketch015
  Type = 0
FEATURE [PartDesign::Body] Body004
  Group = -> [Sketch016,Pad009,Sketch015,Pocket004]
  Origin = -> Origin012
  Tip = -> Pocket004
FEATURE [App::Part] NSV
  Group = -> [LCS_0004,Body004]
  Origin = -> Origin006
FEATURE [App::Link] OCPMDC4mv2001
  AssemblyType = Asm4EE
  AttachedBy = #LCS_0
  AttachedTo = Parent Assembly#LCS_Origin
  LinkedObject = -> OCPMDC4mv2
  expr: Placement = LCS_Origin.Placement * AttachmentOffset * LCS_0.Placement ^ -1
FEATURE [App::Link] OCPRack001  label="OCPRack002"
  AssemblyType = Asm4EE
  AttachedBy = #LCS_0006
  AttachedTo = OCPMDC4mv2001#LCS_0
  AttachmentOffset = pos=(1050,825,1250) rot=(0,0,1;1.5708rad)
  LinkPlacement = pos=(1050,825,1250) rot=(0,0,1;1.5708rad)
  LinkedObject = -> Part
  Placement = pos=(1050,825,1250) rot=(0,0,1;1.5708rad)
  expr: Placement = OCPMDC4mv2001.Placement * LCS_0.Placement * AttachmentOffset * LCS_0006.Placement ^ -1
FEATURE [App::Link] OCPRack001001
  AssemblyType = Asm4EE
  AttachedBy = #LCS_0006
  AttachedTo = OCPRack001#LCS_0006
  AttachmentOffset = pos=(-600,1,0) rot=(0,0,1;0rad)
  LinkPlacement = pos=(1049,225,1250) rot=(0,0,1;1.5708rad)
  LinkedObject = -> Part
  Placement = pos=(1049,225,1250) rot=(0,0,1;1.5708rad)
  expr: Placement = OCPRack001.Placement * LCS_0006.Placement * AttachmentOffset * LCS_0006.Placement ^ -1
FEATURE [App::Link] OCPRack001002
  AssemblyType = Asm4EE
  AttachedBy = #LCS_0006
  AttachedTo = OCPRack001001#LCS_0006
  AttachmentOffset = pos=(-600,0,0) rot=(0,0,1;0rad)
  LinkPlacement = pos=(1049,-375,1250) rot=(0,0,1;1.5708rad)
  LinkedObject = -> Part
  Placement = pos=(1049,-375,1250) rot=(0,0,1;1.5708rad)
  expr: Placement = OCPRack001001.Placement * LCS_0006.Placement * AttachmentOffset * LCS_0006.Placement ^ -1
FEATURE [App::Link] OCPRack001003
  AssemblyType = Asm4EE
  AttachedBy = #LCS_0006
  AttachedTo = OCPRack001002#LCS_0006
  AttachmentOffset = pos=(-600,0,0) rot=(0,0,1;0rad)
  LinkPlacement = pos=(1049,-975,1250) rot=(0,0,1;1.5708rad)
  LinkedObject = -> Part
  Placement = pos=(1049,-975,1250) rot=(0,0,1;1.5708rad)
  expr: Placement = OCPRack001002.Placement * LCS_0006.Placement * AttachmentOffset * LCS_0006.Placement ^ -1
FEATURE [App::Link] OCPRack001004
  AssemblyType = Asm4EE
  AttachedBy = #LCS_0006
  AttachedTo = OCPRack001003#LCS_0006
  AttachmentOffset = pos=(-600,0,0) rot=(0,0,1;0rad)
  LinkPlacement = pos=(1049,-1575,1250) rot=(0,0,1;1.5708rad)
  LinkedObject = -> Part
  Placement = pos=(1049,-1575,1250) rot=(0,0,1;1.5708rad)
  expr: Placement = OCPRack001003.Placement * LCS_0006.Placement * AttachmentOffset * LCS_0006.Placement ^ -1
FEATURE [App::Link] OCPRack001005
  AssemblyType = Asm4EE
  AttachedBy = #LCS_0006
  AttachedTo = OCPMDC4mv2001#LCS_0
  AttachmentOffset = pos=(-1050,825,1250) rot=(0,0,1;1.5708rad)
  LinkPlacement = pos=(-1050,825,1250) rot=(0,0,1;1.5708rad)
  LinkedObject = -> Part
  Placement = pos=(-1050,825,1250) rot=(0,0,1;1.5708rad)
  expr: Placement = OCPMDC4mv2001.Placement * LCS_0.Placement * AttachmentOffset * LCS_0006.Placement ^ -1
FEATURE [App::Link] OCPRack001006
  AssemblyType = Asm4EE
  AttachedBy = #LCS_0006
  AttachedTo = OCPRack001005#LCS_0006
  AttachmentOffset = pos=(-600,0,0) rot=(0,0,1;0rad)
  LinkPlacement = pos=(-1050,225,1250) rot=(0,0,1;1.5708rad)
  LinkedObject = -> Part
  Placement = pos=(-1050,225,1250) rot=(0,0,1;1.5708rad)
  expr: Placement = OCPRack001005.Placement * LCS_0006.Placement * AttachmentOffset * LCS_0006.Placement ^ -1
FEATURE [App::Link] OCPRack001007
  AssemblyType = Asm4EE
  AttachedBy = #LCS_0006
  AttachedTo = OCPRack001006#LCS_0006
  AttachmentOffset = pos=(-600,0,0) rot=(0,0,1;0rad)
  LinkPlacement = pos=(-1050,-375,1250) rot=(0,0,1;1.5708rad)
  LinkedObject = -> Part
  Placement = pos=(-1050,-375,1250) rot=(0,0,1;1.5708rad)
  expr: Placement = OCPRack001006.Placement * LCS_0006.Placement * AttachmentOffset * LCS_0006.Placement ^ -1
FEATURE [App::Link] OCPRack001008
  AssemblyType = Asm4EE
  AttachedBy = #LCS_0006
  AttachedTo = OCPRack001007#LCS_0006
  AttachmentOffset = pos=(-600,0,0) rot=(0,0,1;0rad)
  LinkPlacement = pos=(-1050,-975,1250) rot=(0,0,1;1.5708rad)
  LinkedObject = -> Part
  Placement = pos=(-1050,-975,1250) rot=(0,0,1;1.5708rad)
  expr: Placement = OCPRack001007.Placement * LCS_0006.Placement * AttachmentOffset * LCS_0006.Placement ^ -1
FEATURE [App::Link] OCPRack001009
  AssemblyType = Asm4EE
  AttachedBy = #LCS_0006
  AttachedTo = OCPRack001008#LCS_0006
  AttachmentOffset = pos=(-600,0,0) rot=(0,0,1;0rad)
  LinkPlacement = pos=(-1050,-1575,1250) rot=(0,0,1;1.5708rad)
  LinkedObject = -> Part
  Placement = pos=(-1050,-1575,1250) rot=(0,0,1;1.5708rad)
  expr: Placement = OCPRack001008.Placement * LCS_0006.Placement * AttachmentOffset * LCS_0006.Placement ^ -1
FEATURE [App::Link] Roof001
  AssemblyType = Asm4EE
  AttachedBy = #LCS_0003
  AttachedTo = OCPMDC4mv2001#LCS_0
  AttachmentOffset = pos=(0,0,3650) rot=(0,0,1;0rad)
  LinkPlacement = pos=(0,0,3650) rot=(0,0,1;0rad)
  LinkedObject = -> Roof
  Placement = pos=(0,0,3650) rot=(0,0,1;0rad)
  expr: Placement = OCPMDC4mv2001.Placement * LCS_0.Placement * AttachmentOffset * LCS_0003.Placement ^ -1
FEATURE [App::Link] NSV001
  AssemblyType = Asm4EE
  AttachedBy = #LCS_0004
  AttachedTo = OCPMDC4mv2001#LCS_0
  AttachmentOffset = pos=(800,1550,1250) rot=(0,0,1;3.14159rad)
  LinkPlacement = pos=(800,1550,1250) rot=(0,0,1;3.14159rad)
  LinkedObject = -> NSV
  Placement = pos=(800,1550,1250) rot=(0,0,1;3.14159rad)
  expr: Placement = OCPMDC4mv2001.Placement * LCS_0.Placement * AttachmentOffset * LCS_0004.Placement ^ -1
FEATURE [App::Link] Loeschflasche001
  AssemblyType = Asm4EE
  AttachedBy = #LCS_0005
  AttachedTo = OCPMDC4mv2001#LCS_0
  AttachmentOffset = pos=(-1600,1500,150) rot=(0,0,1;0rad)
  LinkPlacement = pos=(-1600,1500,150) rot=(0,0,1;0rad)
  LinkedObject = -> Loeschflasche
  Placement = pos=(-1600,1500,150) rot=(0,0,1;0rad)
  expr: Placement = OCPMDC4mv2001.Placement * LCS_0.Placement * AttachmentOffset * LCS_0005.Placement ^ -1
FEATURE [PartDesign::CoordinateSystem] LCS_0007
  AttacherType = Attacher::AttachEngine3D
  MapMode = 2
  Support = -> [X_Axis013]
FEATURE [Sketcher::SketchObject] Sketch018
  MapMode = 5
  Placement = pos=(0,0,0) rot=(1,0,0;1.5708rad)
  Support = -> [XZ_Plane014]
  sketch-geometry (8):
    g0: LineSegment StartX=-1500 StartY=500 StartZ=0 EndX=1500 EndY=500 EndZ=0
    g1: LineSegment StartX=1500 StartY=500 StartZ=0 EndX=1500 EndY=-500 EndZ=0
    g2: LineSegment StartX=1500 StartY=-500 StartZ=0 EndX=-1500 EndY=-500 EndZ=0
    g3: LineSegment StartX=-1500 StartY=-500 StartZ=0 EndX=-1500 EndY=500 EndZ=0
    g4: LineSegment StartX=-1450 StartY=450 StartZ=0 EndX=1450 EndY=450 EndZ=0
    g5: LineSegment StartX=1450 StartY=450 StartZ=0 EndX=1450 EndY=-450 EndZ=0
    g6: LineSegment StartX=1450 StartY=-450 StartZ=0 EndX=-1450 EndY=-450 EndZ=0
    g7: LineSegment StartX=-1450 StartY=-450 StartZ=0 EndX=-1450 EndY=450 EndZ=0
  constraints (21):
    c: Coincident(g0,g1)
    c: Coincident(g1,g2)
    c: Coincident(g2,g3)
    c: Coincident(g3,g0)
    c: Horizontal(g2)
    c: Vertical(g3)
    c: Coincident(g4,g5)
    c: Coincident(g5,g6)
    c: Coincident(g6,g7)
    c: Coincident(g7,g4)
    c: Horizontal(g4)
    c: Horizontal(g6)
    c: Vertical(g7)
    c: Symmetric(g0,g0,g-2)
    c: Symmetric(g0,g1,g-1)
    c: DistanceX(g0,g0) = 3000
    c: DistanceY(g1,g1) = 1000
    c: DistanceX(g4,g0) = 50
    c: DistanceY(g4,g0) = 50
    c: Symmetric(g5,g4,g-1)
    c: DistanceX(g0,g4) = 50
FEATURE [PartDesign::Pad] Pad010
  Direction = (1,1,1)
  Length = 200
  Length2 = 100
  Midplane = true
  Placement = pos=(0,0,0) rot=(1,0,0;1.5708rad)
  Profile = -> Sketch018
  Type = 0
FEATURE [Sketcher::SketchObject] Sketch017
  ExternalGeometry = -> [Pad010]
  MapMode = 5
  Placement = pos=(-1450,0,0) rot=(0.707107,0,0.707107;3.14159rad)
  Support = -> [Pad010]
  sketch-geometry (20):
    g0: LineSegment StartX=450 StartY=-100 StartZ=0 EndX=282.18 EndY=100 EndZ=0
    g1: LineSegment StartX=282.18 StartY=100 StartZ=0 EndX=272.18 EndY=100 EndZ=0
    g2: LineSegment StartX=272.18 StartY=100 StartZ=0 EndX=440 EndY=-100 EndZ=0
    g3: LineSegment StartX=440 StartY=-100 StartZ=0 EndX=450 EndY=-100 EndZ=0
    g4: LineSegment StartX=272.18 StartY=-100 StartZ=0 EndX=104.36 EndY=100 EndZ=0
    g5: LineSegment StartX=104.36 StartY=100 StartZ=0 EndX=94.3601 EndY=100 EndZ=0
    g6: LineSegment StartX=94.3601 StartY=100 StartZ=0 EndX=262.18 EndY=-100 EndZ=0
    g7: LineSegment StartX=262.18 StartY=-100 StartZ=0 EndX=272.18 EndY=-100 EndZ=0
    g8: LineSegment StartX=94.3601 StartY=-100 StartZ=0 EndX=-73.4598 EndY=100 EndZ=0
    g9: LineSegment StartX=-73.4598 StartY=100 StartZ=0 EndX=-83.4598 EndY=100 EndZ=0
    g10: LineSegment StartX=-83.4598 StartY=100 StartZ=0 EndX=84.3601 EndY=-100 EndZ=0
    g11: LineSegment StartX=84.3601 StartY=-100 StartZ=0 EndX=94.3601 EndY=-100 EndZ=0
    g12: LineSegment StartX=-83.4598 StartY=-100 StartZ=0 EndX=-251.28 EndY=100 EndZ=0
    g13: LineSegment StartX=-251.28 StartY=100 StartZ=0 EndX=-261.28 EndY=100 EndZ=0
    g14: LineSegment StartX=-261.28 StartY=100 StartZ=0 EndX=-93.4598 EndY=-100 EndZ=0
    g15: LineSegment StartX=-93.4598 StartY=-100 StartZ=0 EndX=-83.4598 EndY=-100 EndZ=0
    g16: LineSegment StartX=-261.28 StartY=-100 StartZ=0 EndX=-429.1 EndY=100 EndZ=0
    g17: LineSegment StartX=-429.1 StartY=100 StartZ=0 EndX=-439.1 EndY=100 EndZ=0
    g18: LineSegment StartX=-439.1 StartY=100 StartZ=0 EndX=-271.28 EndY=-100 EndZ=0
    g19: LineSegment StartX=-271.28 StartY=-100 StartZ=0 EndX=-261.28 EndY=-100 EndZ=0
  constraints (59):
    c: Coincident(g-6,g0)
    c: PointOnObject(g0,g-5)
    c: Coincident(g0,g1)
    c: Coincident(g1,g2)
    c: PointOnObject(g2,g-6)
    c: Coincident(g2,g3)
    c: Coincident(g3,g0)
    c: PointOnObject(g1,g-5)
    c: Parallel(g2,g0)
    c: DistanceX(g1,g1) = 10
    c: PointOnObject(g4,g-6)
    c: PointOnObject(g4,g-5)
    c: Coincident(g4,g5)
    c: PointOnObject(g5,g-5)
    c: Coincident(g5,g6)
    c: PointOnObject(g6,g-6)
    c: Coincident(g6,g7)
    c: PointOnObject(g8,g-6)
    c: PointOnObject(g8,g-5)
    c: Coincident(g8,g9)
    c: PointOnObject(g9,g-5)
    c: Coincident(g9,g10)
    c: PointOnObject(g10,g-6)
    c: Coincident(g10,g11)
    c: PointOnObject(g12,g-6)
    c: PointOnObject(g12,g-5)
    c: Coincident(g12,g13)
    c: PointOnObject(g13,g-5)
    c: Coincident(g13,g14)
    c: Coincident(g14,g15)
    c: Coincident(g15,g12)
    c: Horizontal(g15)
    c: PointOnObject(g16,g-6)
    c: PointOnObject(g16,g-5)
    c: Coincident(g16,g17)
    c: PointOnObject(g17,g-5)
    c: Coincident(g17,g18)
    c: PointOnObject(g18,g-6)
    c: Coincident(g18,g19)
    c: Coincident(g19,g16)
    c: Angle(g2,g-6) = 0.872665
    c: Coincident(g7,g4)
    c: DistanceX(g5,g5) = 10
    c: Parallel(g6,g4)
    c: Angle(g6,g-6) = 0.872665
    c: Vertical(g4,g1)
    c: DistanceX(g9,g9) = 10
    c: Parallel(g10,g8)
    c: Angle(g10,g-6) = 0.872665
    c: Parallel(g14,g12)
    c: Vertical(g11,g5)
    c: Coincident(g8,g11)
    c: DistanceX(g13,g13) = 10
    c: Vertical(g12,g9)
    c: Angle(g-6,g14) = 2.26893
    c: Parallel(g18,g16)
    c: DistanceX(g17,g17) = 10
    c: Vertical(g16,g13)
    c: Angle(g-6,g18) = 2.26893
FEATURE [PartDesign::Pad] Pad011
  BaseFeature = -> Pad010
  Direction = (1,1,1)
  Length = 2900
  Length2 = 100
  Placement = pos=(0,0,0) rot=(1,0,0;1.5708rad)
  Profile = -> Sketch017
  Type = 0
FEATURE [PartDesign::Body] Body005
  Group = -> [Sketch018,Pad010,Sketch017,Pad011]
  Origin = -> Origin014
  Tip = -> Pad011
FEATURE [App::Part] AirBox
  Group = -> [LCS_0007,Body005]
  Origin = -> Origin013
FEATURE [App::Link] AirBox001
  AssemblyType = Asm4EE
  AttachedBy = #LCS_0007
  AttachedTo = OCPMDC4mv2001#LCS_0
  AttachmentOffset = pos=(0,-1900,3000) rot=(0,0,1;0rad)
  LinkPlacement = pos=(0,-1900,3000) rot=(0,0,1;0rad)
  LinkedObject = -> AirBox
  Placement = pos=(0,-1900,3000) rot=(0,0,1;0rad)
  expr: Placement = OCPMDC4mv2001.Placement * LCS_0.Placement * AttachmentOffset * LCS_0007.Placement ^ -1
FEATURE [PartDesign::CoordinateSystem] LCS_0008
  AttacherType = Attacher::AttachEngine3D
  MapMode = 2
  Support = -> [X_Axis015]
FEATURE [Sketcher::SketchObject] Sketch019
  MapMode = 5
  Placement = pos=(0,0,0) rot=(1,0,0;1.5708rad)
  Support = -> [XZ_Plane016]
  sketch-geometry (24):
    g0: LineSegment StartX=0 StartY=-500 StartZ=0 EndX=0 EndY=500 EndZ=0
    g1: LineSegment StartX=0 StartY=500 StartZ=0 EndX=60 EndY=500 EndZ=0
    g2: LineSegment StartX=60 StartY=500 StartZ=0 EndX=60 EndY=-250 EndZ=0
    g3: LineSegment StartX=60 StartY=-250 StartZ=0 EndX=30 EndY=-267.321 EndZ=0
    g4: LineSegment StartX=30 StartY=-267.321 StartZ=0 EndX=60 EndY=-267.321 EndZ=0
    g5: LineSegment StartX=60 StartY=-267.321 StartZ=0 EndX=30 EndY=-284.641 EndZ=0
    g6: LineSegment StartX=30 StartY=-284.641 StartZ=0 EndX=60 EndY=-284.641 EndZ=0
    g7: LineSegment StartX=60 StartY=-284.641 StartZ=0 EndX=30 EndY=-301.962 EndZ=0
    g8: LineSegment StartX=30 StartY=-301.962 StartZ=0 EndX=60 EndY=-301.962 EndZ=0
    g9: LineSegment StartX=60 StartY=-301.962 StartZ=0 EndX=30 EndY=-319.282 EndZ=0
    g10: LineSegment StartX=30 StartY=-319.282 StartZ=0 EndX=60 EndY=-319.282 EndZ=0
    g11: LineSegment StartX=60 StartY=-319.282 StartZ=0 EndX=30 EndY=-336.603 EndZ=0
    g12: LineSegment StartX=30 StartY=-336.603 StartZ=0 EndX=60 EndY=-336.603 EndZ=0
    g13: LineSegment StartX=60 StartY=-336.603 StartZ=0 EndX=30 EndY=-353.923 EndZ=0
    g14: LineSegment StartX=30 StartY=-353.923 StartZ=0 EndX=60 EndY=-353.923 EndZ=0
    g15: LineSegment StartX=60 StartY=-353.923 StartZ=0 EndX=30 EndY=-371.244 EndZ=0
    g16: LineSegment StartX=30 StartY=-371.244 StartZ=0 EndX=60 EndY=-371.244 EndZ=0
    g17: LineSegment StartX=60 StartY=-371.244 StartZ=0 EndX=30 EndY=-388.564 EndZ=0
    g18: LineSegment StartX=30 StartY=-388.564 StartZ=0 EndX=60 EndY=-388.564 EndZ=0
    g19: LineSegment StartX=60 StartY=-388.564 StartZ=0 EndX=30 EndY=-405.885 EndZ=0
    g20: LineSegment StartX=30 StartY=-405.885 StartZ=0 EndX=60 EndY=-405.885 EndZ=0
    g21: LineSegment StartX=60 StartY=-405.885 StartZ=0 EndX=30 EndY=-423.205 EndZ=0
    g22: LineSegment StartX=30 StartY=-423.205 StartZ=0 EndX=60 EndY=-423.205 EndZ=0
    g23: LineSegment StartX=60 StartY=-423.205 StartZ=0 EndX=0 EndY=-500 EndZ=0
  constraints (72):
    c: Vertical(g0)
    c: Coincident(g0,g1)
    c: Horizontal(g1)
    c: Coincident(g1,g2)
    c: Vertical(g2)
    c: Coincident(g2,g3)
    c: Coincident(g3,g4)
    c: Coincident(g4,g5)
    c: Coincident(g5,g6)
    c: Coincident(g6,g7)
    c: Coincident(g7,g8)
    c: Horizontal(g8)
    c: Coincident(g8,g9)
    c: Coincident(g9,g10)
    c: Coincident(g10,g11)
    c: Coincident(g11,g12)
    c: Coincident(g12,g13)
    c: Coincident(g13,g14)
    c: Coincident(g14,g15)
    c: Coincident(g15,g16)
    c: Coincident(g16,g17)
    c: Coincident(g17,g18)
    c: Coincident(g18,g19)
    c: Coincident(g19,g20)
    c: Coincident(g20,g21)
    c: Coincident(g21,g22)
    c: Vertical(g4,g6)
    c: Vertical(g6,g8)
    c: Vertical(g8,g10)
    c: Vertical(g10,g12)
    c: Vertical(g12,g14)
    c: Vertical(g14,g16)
    c: Vertical(g16,g18)
    c: Vertical(g18,g20)
    c: Vertical(g20,g22)
    c: Vertical(g3,g5)
    c: Vertical(g5,g7)
    c: Vertical(g7,g9)
    c: Vertical(g9,g11)
    c: Vertical(g11,g13)
    c: Vertical(g13,g15)
    c: Vertical(g15,g17)
    c: Vertical(g17,g19)
    c: Vertical(g19,g21)
    c: Angle(g4,g3) = 0.523599
    c: Angle(g6,g5) = 0.523599
    c: Angle(g4,g5) = 0.523599
    c: Angle(g6,g7) = 0.523599
    c: Angle(g8,g7) = 0.523599
    c: DistanceX(g3,g4) = 30
    c: Angle(g8,g9) = 0.523599
    c: Angle(g10,g9) = 0.523599
    c: Angle(g12,g11) = 0.523599
    c: Angle(g10,g11) = 0.523599
    c: Angle(g12,g13) = 0.523599
    c: Angle(g14,g13) = 0.523599
    c: Angle(g14,g15) = 0.523599
    c: Angle(g16,g15) = 0.523599
    c: Angle(g16,g17) = 0.523599
    c: Angle(g18,g17) = 0.523599
    c: Angle(g18,g19) = 0.523599
    c: Angle(g20,g19) = 0.523599
    c: Angle(g20,g21) = 0.523599
    c: Angle(g22,g21) = 0.523599
    c: DistanceY(g0,g0) = 1000
    c: Coincident(g23,g22)
    c: Coincident(g23,g0)
    c: DistanceY(g-1,g0) = 500
    c: Vertical(g2,g4)
    c: DistanceX(g0,g1) = 60
    c: PointOnObject(g-1,g0)
    c: DistanceY(g2,g1) = 750
FEATURE [PartDesign::Revolution] Revolution001
  Angle = 360
  Axis = (0,-2e-16,1)
  Base = (0,0,0)
  Placement = pos=(0,0,0) rot=(1,0,0;1.5708rad)
  Profile = -> Sketch019
  ReferenceAxis = -> Sketch019 [V_Axis]
  Reversed = true
FEATURE [Sketcher::SketchObject] Sketch020
  MapMode = 5
  Placement = pos=(0,0,500) rot=(0,0,1;3.14159rad)
  Support = -> [Revolution001]
  sketch-geometry (8):
    g0: LineSegment StartX=-109.659 StartY=-60 StartZ=0 EndX=-109.659 EndY=60 EndZ=0
    g1: LineSegment StartX=-109.659 StartY=60 StartZ=0 EndX=-60 EndY=109.659 EndZ=0
    g2: LineSegment StartX=-60 StartY=109.659 StartZ=0 EndX=60 EndY=109.659 EndZ=0
    g3: LineSegment StartX=60 StartY=109.659 StartZ=0 EndX=109.659 EndY=60 EndZ=0
    g4: LineSegment StartX=109.659 StartY=60 StartZ=0 EndX=109.659 EndY=-60 EndZ=0
    g5: LineSegment StartX=109.659 StartY=-60 StartZ=0 EndX=60 EndY=-109.659 EndZ=0
    g6: LineSegment StartX=60 StartY=-109.659 StartZ=0 EndX=-60 EndY=-109.659 EndZ=0
    g7: LineSegment StartX=-60 StartY=-109.659 StartZ=0 EndX=-109.659 EndY=-60 EndZ=0
  constraints (21):
    c: Vertical(g0)
    c: Coincident(g0,g1)
    c: Coincident(g1,g2)
    c: Coincident(g2,g3)
    c: Coincident(g3,g4)
    c: Coincident(g4,g5)
    c: Coincident(g5,g6)
    c: Coincident(g6,g7)
    c: Coincident(g7,g0)
    c: Symmetric(g2,g1,g-2)
    c: Symmetric(g3,g4,g-1)
    c: Symmetric(g5,g6,g-2)
    c: DistanceY(g4,g4) = 120
    c: DistanceX(g6,g6) = 120
    c: DistanceY(g0,g0) = 120
    c: DistanceX(g2,g2) = 120
    c: Angle(g2,g3) = 2.35619
    c: Angle(g4,g5) = 2.35619
    c: Angle(g6,g7) = 2.35619
    c: Angle(g0,g1) = 2.35619
    c: Distance(g-1,g2) = 125
FEATURE [PartDesign::Pad] Pad012
  BaseFeature = -> Revolution001
  Direction = (1,1,1)
  Length = 20
  Length2 = 100
  Placement = pos=(0,0,0) rot=(1,0,0;1.5708rad)
  Profile = -> Sketch020
  Type = 0
FEATURE [PartDesign::Body] Body006
  Group = -> [Sketch019,Revolution001,Sketch020,Pad012]
  Origin = -> Origin016
  Tip = -> Pad012
FEATURE [App::Part] Schraubenfundament
  Group = -> [LCS_0008,Body006]
  Origin = -> Origin015
FEATURE [App::Link] Schraubenfundament001
  AssemblyType = Asm4EE
  AttachedBy = #LCS_0008
  AttachedTo = OCPMDC4mv2001#LCS_0
  AttachmentOffset = pos=(1425,-1680,-870) rot=(0,0,1;0rad)
  LinkPlacement = pos=(1425,-1680,-870) rot=(0,0,1;0rad)
  LinkedObject = -> Schraubenfundament
  Placement = pos=(1425,-1680,-870) rot=(0,0,1;0rad)
  expr: Placement = OCPMDC4mv2001.Placement * LCS_0.Placement * AttachmentOffset * LCS_0008.Placement ^ -1
FEATURE [App::Link] Schraubenfundament002
  AssemblyType = Asm4EE
  AttachedBy = #LCS_0008
  AttachedTo = Schraubenfundament001#LCS_0008
  AttachmentOffset = pos=(-750,0,0) rot=(0,0,1;0rad)
  LinkPlacement = pos=(675,-1680,-870) rot=(0,0,1;0rad)
  LinkedObject = -> Schraubenfundament
  Placement = pos=(675,-1680,-870) rot=(0,0,1;0rad)
  expr: Placement = Schraubenfundament001.Placement * LCS_0008.Placement * AttachmentOffset * LCS_0008.Placement ^ -1
FEATURE [App::Link] Schraubenfundament003
  AssemblyType = Asm4EE
  AttachedBy = #LCS_0008
  AttachedTo = Schraubenfundament002#LCS_0008
  AttachmentOffset = pos=(-1350,0,0) rot=(0,0,1;0rad)
  LinkPlacement = pos=(-675,-1680,-870) rot=(0,0,1;0rad)
  LinkedObject = -> Schraubenfundament
  Placement = pos=(-675,-1680,-870) rot=(0,0,1;0rad)
  expr: Placement = Schraubenfundament002.Placement * LCS_0008.Placement * AttachmentOffset * LCS_0008.Placement ^ -1
FEATURE [App::Link] Schraubenfundament004
  AssemblyType = Asm4EE
  AttachedBy = #LCS_0008
  AttachedTo = Schraubenfundament003#LCS_0008
  AttachmentOffset = pos=(-750,0,0) rot=(0,0,1;0rad)
  LinkPlacement = pos=(-1425,-1680,-870) rot=(0,0,1;0rad)
  LinkedObject = -> Schraubenfundament
  Placement = pos=(-1425,-1680,-870) rot=(0,0,1;0rad)
  expr: Placement = Schraubenfundament003.Placement * LCS_0008.Placement * AttachmentOffset * LCS_0008.Placement ^ -1
FEATURE [App::Link] Schraubenfundament005
  AssemblyType = Asm4EE
  AttachedBy = #LCS_0008
  AttachedTo = Schraubenfundament001#LCS_0008
  AttachmentOffset = pos=(0,3360,0) rot=(0,0,1;0rad)
  LinkPlacement = pos=(1425,1680,-870) rot=(0,0,1;0rad)
  LinkedObject = -> Schraubenfundament
  Placement = pos=(1425,1680,-870) rot=(0,0,1;0rad)
  expr: Placement = Schraubenfundament001.Placement * LCS_0008.Placement * AttachmentOffset * LCS_0008.Placement ^ -1
FEATURE [App::Link] Schraubenfundament006
  AssemblyType = Asm4EE
  AttachedBy = #LCS_0008
  AttachedTo = Schraubenfundament002#LCS_0008
  AttachmentOffset = pos=(0,3360,0) rot=(0,0,1;0rad)
  LinkPlacement = pos=(675,1680,-870) rot=(0,0,1;0rad)
  LinkedObject = -> Schraubenfundament
  Placement = pos=(675,1680,-870) rot=(0,0,1;0rad)
  expr: Placement = Schraubenfundament002.Placement * LCS_0008.Placement * AttachmentOffset * LCS_0008.Placement ^ -1
FEATURE [App::Link] Schraubenfundament007
  AssemblyType = Asm4EE
  AttachedBy = #LCS_0008
  AttachedTo = Schraubenfundament003#LCS_0008
  AttachmentOffset = pos=(0,3360,0) rot=(0,0,1;0rad)
  LinkPlacement = pos=(-675,1680,-870) rot=(0,0,1;0rad)
  LinkedObject = -> Schraubenfundament
  Placement = pos=(-675,1680,-870) rot=(0,0,1;0rad)
  expr: Placement = Schraubenfundament003.Placement * LCS_0008.Placement * AttachmentOffset * LCS_0008.Placement ^ -1
FEATURE [App::Link] Schraubenfundament008
  AssemblyType = Asm4EE
  AttachedBy = #LCS_0008
  AttachedTo = Schraubenfundament004#LCS_0008
  AttachmentOffset = pos=(0,3360,0) rot=(0,0,1;0rad)
  LinkPlacement = pos=(-1425,1680,-870) rot=(0,0,1;0rad)
  LinkedObject = -> Schraubenfundament
  Placement = pos=(-1425,1680,-870) rot=(0,0,1;0rad)
  expr: Placement = Schraubenfundament004.Placement * LCS_0008.Placement * AttachmentOffset * LCS_0008.Placement ^ -1
FEATURE [Part::Feature] Part__Feature006  label="Blade005"
  Placement = pos=(2e-15,1e-15,0) rot=(0,0,1;1.0472rad)
  shape: bbox 5.916 x 6.687 x 3.511 mm, 14 faces (baked)
FEATURE [Part::Feature] Part__Feature005  label="Blade004"
  Placement = pos=(0,1e-15,0) rot=(0,0,1;2.0944rad)
  shape: bbox 7.511 x 4.39 x 3.511 mm, 14 faces (baked)
FEATURE [Part::Feature] Part__Feature  label="Geh㴳e"
  shape: bbox 16.82 x 4 x 16.82 mm, 62 faces (baked)
FEATURE [Part::Feature] Part__Feature002  label="Blade001"
  Placement = pos=(0,0,0) rot=(0,0,-1;1.0472rad)
  shape: bbox 7.511 x 4.39 x 3.511 mm, 14 faces (baked)
FEATURE [Part::Feature] Part__Feature003  label="Blade002"
  Placement = pos=(0,0,0) rot=(0,0,-1;2.0944rad)
  shape: bbox 5.916 x 6.687 x 3.511 mm, 14 faces (baked)
FEATURE [Part::Feature] Part__Feature001  label="Blade"
  shape: bbox 4.292 x 7.417 x 3.511 mm, 14 faces (baked)
FEATURE [Part::Feature] Part__Feature004  label="Blade003"
  Placement = pos=(0,0,0) rot=(0,0,1;3.14159rad)
  shape: bbox 4.292 x 7.417 x 3.511 mm, 14 faces (baked)
FEATURE [App::Part] Propeller
  Group = -> [Part__Feature001,Part__Feature002,Part__Feature003,Part__Feature004,Part__Feature005,Part__Feature006]
  Origin = -> Origin017
  Placement = pos=(0,-3.9,0) rot=(-1,0,0;1.5708rad)
FEATURE [App::Part] Baugruppe
  Group = -> [Part__Feature,Propeller]
  Origin = -> Origin018
FEATURE [Part::FeaturePython] Clone002  label="Baugruppe003"  # WARN: FeaturePython — macro-defined, semantics opaque (R4)
  AttacherType = Attacher::AttachEngine3D
  Fuse = false
  Scale = (50,20,50)
FEATURE [App::Part] Fan750mm
  Group = -> [LCS_0002,Clone002,Baugruppe]
  Origin = -> Origin004
FEATURE [App::Link] Fan750mm001
  AssemblyType = Asm4EE
  AttachedBy = #LCS_0002
  AttachedTo = OCPMDC4mv2001#LCS_0
  AttachmentOffset = pos=(1900,500,3000) rot=(0,0,1;1.5708rad)
  LinkPlacement = pos=(1900,500,3000) rot=(0,0,1;1.5708rad)
  LinkedObject = -> Fan750mm
  Placement = pos=(1900,500,3000) rot=(0,0,1;1.5708rad)
  expr: Placement = OCPMDC4mv2001.Placement * LCS_0.Placement * AttachmentOffset * LCS_0002.Placement ^ -1
FEATURE [App::Link] Fan750mm002
  AssemblyType = Asm4EE
  AttachedBy = #LCS_0002
  AttachedTo = Fan750mm001#LCS_0002
  AttachmentOffset = pos=(-1500,0,0) rot=(0,0,1;0rad)
  LinkPlacement = pos=(1900,-1000,3000) rot=(0,0,1;1.5708rad)
  LinkedObject = -> Fan750mm
  Placement = pos=(1900,-1000,3000) rot=(0,0,1;1.5708rad)
  expr: Placement = Fan750mm001.Placement * LCS_0002.Placement * AttachmentOffset * LCS_0002.Placement ^ -1
FEATURE [App::Link] Fan750mm003
  AssemblyType = Asm4EE
  AttachedBy = #LCS_0002
  AttachedTo = OCPMDC4mv2001#LCS_0
  AttachmentOffset = pos=(-1900,500,3000) rot=(0,0,1;4.71239rad)
  LinkPlacement = pos=(-1900,500,3000) rot=(0,0,1;4.71239rad)
  LinkedObject = -> Fan750mm
  Placement = pos=(-1900,500,3000) rot=(0,0,1;4.71239rad)
  expr: Placement = OCPMDC4mv2001.Placement * LCS_0.Placement * AttachmentOffset * LCS_0002.Placement ^ -1
FEATURE [App::Link] Fan750mm004
  AssemblyType = Asm4EE
  AttachedBy = #LCS_0002
  AttachedTo = Fan750mm003#LCS_0002
  AttachmentOffset = pos=(1500,0,0) rot=(0,0,1;0rad)
  LinkPlacement = pos=(-1900,-1000,3000) rot=(0,0,1;4.71239rad)
  LinkedObject = -> Fan750mm
  Placement = pos=(-1900,-1000,3000) rot=(0,0,1;4.71239rad)
  expr: Placement = Fan750mm003.Placement * LCS_0002.Placement * AttachmentOffset * LCS_0002.Placement ^ -1
FEATURE [App::MeasureDistance] Distance  label="Distance: 3000.03 mm"
  Distance = 3000.03
  P1 = (1498.71,1125,3637.44)
  P2 = (1498.71,-1875,3650)
FEATURE [App::MeasureDistance] Distance001  label="Distance: 1200.01 mm"
  Distance = 1200.01
  P1 = (600,742.847,2350)
  P2 = (-600,737.643,2350)
FEATURE [App::MeasureDistance] Distance002  label="Distance: 1288.14 mm"
  Distance = 1288.14
  P1 = (1293.36,1090.02,2350)
  P2 = (1317.59,1125,3637.44)
FEATURE [PartDesign::CoordinateSystem] LCS_0009
  AttacherType = Attacher::AttachEngine3D
  MapMode = 2
  Support = -> [X_Axis019]
FEATURE [Part::Feature] Part__Feature007  label="Blade006"
  Placement = pos=(2e-15,1e-15,0) rot=(0,0,1;1.0472rad)
  shape: bbox 5.916 x 6.687 x 3.511 mm, 14 faces (baked)
FEATURE [Part::Feature] Part__Feature008  label="Blade007"
  Placement = pos=(0,1e-15,0) rot=(0,0,1;2.0944rad)
  shape: bbox 7.511 x 4.39 x 3.511 mm, 14 faces (baked)
FEATURE [Part::Feature] Part__Feature009  label="Geh㴳e001"
  shape: bbox 16.82 x 4 x 16.82 mm, 62 faces (baked)
FEATURE [Part::Feature] Part__Feature010  label="Blade008"
  Placement = pos=(0,0,0) rot=(0,0,-1;1.0472rad)
  shape: bbox 7.511 x 4.39 x 3.511 mm, 14 faces (baked)
FEATURE [Part::Feature] Part__Feature011  label="Blade009"
  Placement = pos=(0,0,0) rot=(0,0,-1;2.0944rad)
  shape: bbox 5.916 x 6.687 x 3.511 mm, 14 faces (baked)
FEATURE [Part::Feature] Part__Feature012  label="Blade010"
  shape: bbox 4.292 x 7.417 x 3.511 mm, 14 faces (baked)
FEATURE [Part::Feature] Part__Feature013  label="Blade011"
  Placement = pos=(0,0,0) rot=(0,0,1;3.14159rad)
  shape: bbox 4.292 x 7.417 x 3.511 mm, 14 faces (baked)
FEATURE [App::Part] Propeller001
  Group = -> [Part__Feature012,Part__Feature010,Part__Feature011,Part__Feature013,Part__Feature008,Part__Feature007]
  Origin = -> Origin020
  Placement = pos=(0,-3.9,0) rot=(-1,0,0;1.5708rad)
FEATURE [App::Part] Baugruppe001
  Group = -> [Part__Feature009,Propeller001]
  Origin = -> Origin021
FEATURE [Part::FeaturePython] Clone003  label="Baugruppe005"  # WARN: FeaturePython — macro-defined, semantics opaque (R4)
  AttacherType = Attacher::AttachEngine3D
  Fuse = false
  Scale = (70,16,70)
FEATURE [App::Part] Fan1000mm
  Group = -> [LCS_0009,Clone003,Baugruppe001]
  Origin = -> Origin019
FEATURE [PartDesign::CoordinateSystem] LCS_0010
  AttacherType = Attacher::AttachEngine3D
  MapMode = 2
  Support = -> [X_Axis022]
FEATURE [Sketcher::SketchObject] Sketch021
  MapMode = 5
  Support = -> [XY_Plane023]
  sketch-geometry (6):
    g0: LineSegment StartX=-700 StartY=1500 StartZ=0 EndX=700 EndY=1500 EndZ=0
    g1: LineSegment StartX=700 StartY=1500 StartZ=0 EndX=700 EndY=-1500 EndZ=0
    g2: LineSegment StartX=700 StartY=-1500 StartZ=0 EndX=-700 EndY=-1500 EndZ=0
    g3: LineSegment StartX=-700 StartY=-1500 StartZ=0 EndX=-700 EndY=1500 EndZ=0
    g4: Circle CenterX=0 CenterY=850 CenterZ=0 NormalX=0 NormalY=0 NormalZ=1 AngleXU=0 Radius=505
    g5: Circle CenterX=0 CenterY=-650 CenterZ=0 NormalX=0 NormalY=0 NormalZ=1 AngleXU=0 Radius=505
  constraints (16):
    c: Coincident(g0,g1)
    c: Coincident(g1,g2)
    c: Coincident(g2,g3)
    c: Coincident(g3,g0)
    c: Horizontal(g2)
    c: Vertical(g3)
    c: DistanceY(g1,g1) = 3000
    c: DistanceX(g0,g0) = 1400
    c: Symmetric(g0,g0,g-2)
    c: Symmetric(g0,g1,g-1)
    c: PointOnObject(g4,g-2)
    c: PointOnObject(g5,g-2)
    c: Equal(g4,g5)
    c: Radius(g4) = 505
    c: DistanceY(g5,g4) = 1500
    c: DistanceY(g-1,g4) = 850
FEATURE [PartDesign::Pad] Pad013
  Direction = (1,1,1)
  Length = 20
  Length2 = 100
  Profile = -> Sketch021
  Type = 0
FEATURE [PartDesign::Body] Body007
  Group = -> [Sketch021,Pad013]
  Origin = -> Origin023
  Tip = -> Pad013
FEATURE [App::Part] OCPceiling
  Group = -> [LCS_0010,Body007]
  Origin = -> Origin022
FEATURE [App::Link] OCPceiling001
  AssemblyType = Asm4EE
  AttachedBy = #LCS_0010
  AttachedTo = OCPMDC4mv2001#LCS_0
  AttachmentOffset = pos=(0,-375,2350) rot=(0,0,1;0rad)
  LinkPlacement = pos=(0,-375,2350) rot=(0,0,1;0rad)
  LinkedObject = -> OCPceiling
  Placement = pos=(0,-375,2350) rot=(0,0,1;0rad)
  expr: Placement = OCPMDC4mv2001.Placement * LCS_0.Placement * AttachmentOffset * LCS_0010.Placement ^ -1
FEATURE [App::Link] OCPceiling002
  AssemblyType = Asm4EE
  AttachedBy = #LCS_0010
  AttachedTo = OCPceiling001#LCS_0010
  LinkPlacement = pos=(0,-375,2350) rot=(0,0,1;0rad)
  LinkedObject = -> OCPceiling
  Placement = pos=(0,-375,2350) rot=(0,0,1;0rad)
  expr: Placement = OCPceiling001.Placement * LCS_0010.Placement * AttachmentOffset * LCS_0010.Placement ^ -1
FEATURE [App::Link] Fan1000mm001
  AssemblyType = Asm4EE
  AttachedBy = #LCS_0009
  AttachedTo = OCPceiling002#LCS_0010
  AttachmentOffset = pos=(0,-650,80) rot=(-0.57735,0.57735,0.57735;4.18879rad)
  LinkPlacement = pos=(0,-1025,2430) rot=(-0.57735,0.57735,0.57735;4.18879rad)
  LinkedObject = -> Fan1000mm
  Placement = pos=(0,-1025,2430) rot=(-0.57735,0.57735,0.57735;4.18879rad)
  expr: Placement = OCPceiling002.Placement * LCS_0010.Placement * AttachmentOffset * LCS_0009.Placement ^ -1
FEATURE [App::Link] Fan1000mm002
  AssemblyType = Asm4EE
  AttachedBy = #LCS_0009
  AttachedTo = Fan1000mm001#LCS_0009
  AttachmentOffset = pos=(-1500,0,0) rot=(0,0,1;0rad)
  LinkPlacement = pos=(0,475,2430) rot=(-0.57735,0.57735,0.57735;4.18879rad)
  LinkedObject = -> Fan1000mm
  Placement = pos=(0,475,2430) rot=(-0.57735,0.57735,0.57735;4.18879rad)
  expr: Placement = Fan1000mm001.Placement * LCS_0009.Placement * AttachmentOffset * LCS_0009.Placement ^ -1
FEATURE [PartDesign::CoordinateSystem] LCS_0011
  AttacherType = Attacher::AttachEngine3D
  MapMode = 2
  Support = -> [X_Axis024]
FEATURE [Sketcher::SketchObject] Sketch024
  MapMode = 5
  Placement = pos=(0,0,0) rot=(1,0,0;1.5708rad)
  Support = -> [XZ_Plane025]
  sketch-geometry (8):
    g0: LineSegment StartX=-80 StartY=0 StartZ=0 EndX=80 EndY=0 EndZ=0
    g1: LineSegment StartX=80 StartY=0 StartZ=0 EndX=80 EndY=15 EndZ=0
    g2: LineSegment StartX=-80 StartY=15 StartZ=0 EndX=-80 EndY=0 EndZ=0
    g3: LineSegment StartX=-7.5 StartY=15 StartZ=0 EndX=-7.5 EndY=1280 EndZ=0
    g4: LineSegment StartX=-7.5 StartY=1280 StartZ=0 EndX=7.5 EndY=1280 EndZ=0
    g5: LineSegment StartX=7.5 StartY=1280 StartZ=0 EndX=7.5 EndY=15 EndZ=0
    g6: LineSegment StartX=-80 StartY=15 StartZ=0 EndX=-7.5 EndY=15 EndZ=0
    g7: LineSegment StartX=7.5 StartY=15 StartZ=0 EndX=80 EndY=15 EndZ=0
  constraints (22):
    c: Coincident(g0,g1)
    c: Coincident(g2,g0)
    c: Vertical(g1)
    c: Vertical(g2)
    c: PointOnObject(g0,g-1)
    c: Coincident(g3,g4)
    c: Coincident(g4,g5)
    c: Horizontal(g4)
    c: Vertical(g3)
    c: Vertical(g5)
    c: Symmetric(g5,g3,g-2)
    c: DistanceY(g1,g1) = 15
    c: Coincident(g6,g2)
    c: Coincident(g6,g3)
    c: Horizontal(g6)
    c: Coincident(g7,g5)
    c: Coincident(g7,g1)
    c: Horizontal(g7)
    c: Symmetric(g0,g0,g-2)
    c: DistanceX(g3,g5) = 15
    c: DistanceX(g0,g0) = 160
    c: DistanceY(g-1,g4) = 1280
FEATURE [PartDesign::Pad] Pad014
  Direction = (1,1,1)
  Length = 3000
  Length2 = 100
  Midplane = true
  Placement = pos=(0,0,0) rot=(1,0,0;1.5708rad)
  Profile = -> Sketch024
  Type = 0
FEATURE [Sketcher::SketchObject] Sketch022
  ExternalGeometry = -> [Pad014]
  MapMode = 5
  Placement = pos=(7.5,0,0) rot=(0.707107,0,0.707107;3.14159rad)
  Support = -> [Pad014]
  sketch-geometry (4):
    g0: LineSegment StartX=350 StartY=-1150 StartZ=0 EndX=1000 EndY=-1150 EndZ=0
    g1: LineSegment StartX=1000 StartY=-1150 StartZ=0 EndX=1000 EndY=1150 EndZ=0
    g2: LineSegment StartX=1000 StartY=1150 StartZ=0 EndX=350 EndY=1150 EndZ=0
    g3: LineSegment StartX=350 StartY=1150 StartZ=0 EndX=350 EndY=-1150 EndZ=0
  constraints (12):
    c: Coincident(g0,g1)
    c: Coincident(g1,g2)
    c: Coincident(g2,g3)
    c: Coincident(g3,g0)
    c: Horizontal(g0)
    c: Horizontal(g2)
    c: Vertical(g1)
    c: Vertical(g3)
    c: DistanceX(g-3,g2) = 350
    c: DistanceY(g-4,g0) = 350
    c: DistanceY(g2,g-3) = 350
    c: DistanceX(g2,g2) = 650
FEATURE [PartDesign::Pocket] Pocket005
  BaseFeature = -> Pad014
  Length = 5
  Length2 = 100
  Placement = pos=(0,0,0) rot=(1,0,0;1.5708rad)
  Profile = -> Sketch022
  Type = 1
FEATURE [Sketcher::SketchObject] Sketch023
  ExternalGeometry = -> [Pocket005]
  MapMode = 5
  Placement = pos=(0,1150,-2.53e-13) rot=(1,0,0;1.5708rad)
  Support = -> [Pocket005]
  sketch-geometry (4):
    g0: LineSegment StartX=-7.5 StartY=1000 StartZ=0 EndX=7.5 EndY=1000 EndZ=0
    g1: LineSegment StartX=7.5 StartY=1000 StartZ=0 EndX=-218.819 EndY=365.437 EndZ=0
    g2: LineSegment StartX=-218.819 StartY=365.437 StartZ=0 EndX=-231.597 EndY=371.667 EndZ=0
    g3: LineSegment StartX=-231.597 StartY=371.667 StartZ=0 EndX=-7.5 EndY=1000 EndZ=0
  constraints (8):
    c: Coincident(g-4,g0)
    c: Coincident(g0,g-3)
    c: Coincident(g0,g1)
    c: Coincident(g1,g2)
    c: Coincident(g2,g3)
    c: Coincident(g3,g0)
    c: Parallel(g3,g1)
    c: Distance(g3) = 667.1
FEATURE [PartDesign::Pad] Pad015
  BaseFeature = -> Pocket005
  Direction = (1,1,1)
  Length = 2300
  Length2 = 100
  Placement = pos=(0,0,0) rot=(1,0,0;1.5708rad)
  Profile = -> Sketch023
  Type = 0
FEATURE [PartDesign::Body] Body008
  Group = -> [Sketch024,Pad014,Sketch022,Pocket005,Sketch023,Pad015]
  Origin = -> Origin025
  Tip = -> Pad015
FEATURE [App::Part] HotColdSeperator
  Group = -> [LCS_0011,Body008]
  Origin = -> Origin024
FEATURE [App::Link] HotColdSeperator001
  AssemblyType = Asm4EE
  AttachedBy = #LCS_0011
  AttachedTo = OCPMDC4mv2001#LCS_0
  AttachmentOffset = pos=(1200,-375,2350) rot=(0,0,1;0rad)
  LinkPlacement = pos=(1200,-375,2350) rot=(0,0,1;0rad)
  LinkedObject = -> HotColdSeperator
  Placement = pos=(1200,-375,2350) rot=(0,0,1;0rad)
  expr: Placement = OCPMDC4mv2001.Placement * LCS_0.Placement * AttachmentOffset * LCS_0011.Placement ^ -1
FEATURE [App::Link] HotColdSeperator002
  AssemblyType = Asm4EE
  AttachedBy = #LCS_0011
  AttachedTo = HotColdSeperator001#LCS_0011
  AttachmentOffset = pos=(-2400,0,0) rot=(0,0,1;3.14159rad)
  LinkPlacement = pos=(-1200,-375,2350) rot=(0,0,1;3.14159rad)
  LinkedObject = -> HotColdSeperator
  Placement = pos=(-1200,-375,2350) rot=(0,0,1;3.14159rad)
  expr: Placement = HotColdSeperator001.Placement * LCS_0011.Placement * AttachmentOffset * LCS_0011.Placement ^ -1
FEATURE [PartDesign::CoordinateSystem] LCS_0012
  AttacherType = Attacher::AttachEngine3D
  MapMode = 2
  Support = -> [X_Axis026]
FEATURE [Part::Feature] Part__Feature014  label="5. Base All"
  Placement = pos=(2.5,48.05,21.325) rot=(0,1,0;3.14159rad)
  shape: bbox 75.8 x 5 x 75 mm, 92 faces (baked)
FEATURE [Part::Feature] Part__Feature030  label="RRA.1 Horn Bintang Standar"
  Placement = pos=(-60.8942,73.25,-2.78742) rot=(-0.427779,-0.639142,0.639142;3.95004rad)
  shape: bbox 32.88 x 6 x 30.95 mm, 87 faces (baked)
FEATURE [Part::Feature] Part__Feature031  label="RRA.1 - Servo Tower Pro MG995"
  Placement = pos=(-52.0692,118.8,-2.78742) rot=(1,0,0;3.14159rad)
  shape: bbox 54.65 x 45.95 x 21.65 mm, 299 faces (baked)
FEATURE [Part::Feature] Part__Feature037  label="Horn Bintang Standar001"
  Placement = pos=(-14.85,89.2902,8.82146) rot=(0.357407,0.862856,0.357407;1.71777rad)
  shape: bbox 5.85 x 30.26 x 30.26 mm, 78 faces (baked)
FEATURE [Part::Feature] Part__Feature038  label="Horn Bintang Standar002"
  Placement = pos=(0,45.7,8.825) rot=(0,0.707107,0.707107;3.14159rad)
  shape: bbox 31.15 x 5.85 x 27.64 mm, 78 faces (baked)
FEATURE [Part::Feature] Part__Feature039  label="Horn Lingkaran Standar"
  Placement = pos=(-2.5,89.3089,-221.155) rot=(0.707107,0.707107,9.1e-05;3.14177rad)
  shape: bbox 20.95 x 20.95 x 5.854 mm, 47 faces (baked)
FEATURE [Part::Feature] Part__Feature032  label="Servo - Tower Pro MG995"
  Placement = pos=(63.55,83.05,15.0617) rot=(-0.678598,0.678598,-0.281085;3.68962rad)
  shape: bbox 45.7 x 51.04 x 51.04 mm, 299 faces (baked)
FEATURE [Part::Feature] Part__Feature040  label="3. Link Arm Servo 2B"
  Placement = pos=(13,89.2902,8.82146) rot=(0,0.923911,-0.382607;3.14159rad)
  shape: bbox 5 x 50.78 x 50.79 mm, 47 faces (baked)
FEATURE [Part::Feature] Part__Feature041  label="4. Connector 1"
  Placement = pos=(-22,153.49,-143.756) rot=(0,0.92388,-0.382683;3.14159rad)
  shape: bbox 3 x 101.9 x 101.9 mm, 15 faces (baked)
FEATURE [Part::Feature] Part__Feature033  label="Servo - Tower Pro MG996"
  Placement = pos=(-60.55,83.05,15.0617) rot=(-0.357407,-0.357407,-0.862856;1.71777rad)
  shape: bbox 45.7 x 51.04 x 51.04 mm, 299 faces (baked)
FEATURE [Part::Feature] Part__Feature034  label="Servo - Tower Pro MG997"
  Placement = pos=(0,0,0) rot=(0,1,0;1.5708rad)
  shape: bbox 21.65 x 45.7 x 54.65 mm, 299 faces (baked)
FEATURE [Part::Feature] Part__Feature035  label="Servo - Tower Pro MG998"
  Placement = pos=(-2.5,98.1221,-175.453) rot=(-0.577301,-0.577449,0.577301;2.09425rad)
  shape: bbox 21.65 x 54.65 x 45.71 mm, 299 faces (baked)
FEATURE [Part::Feature] Part__Feature036  label="Horn Bintang Standar"
  Placement = pos=(17.85,89.2902,8.82146) rot=(0.520029,-0.677599,-0.520029;1.95053rad)
  shape: bbox 5.85 x 30.26 x 30.25 mm, 78 faces (baked)
FEATURE [Part::Feature] Part__Feature023  label="[Fix 1] 1.Ref - Capit 008"
  Placement = pos=(-58.5526,69.25,48.5827) rot=(0.401494,0.647612,-0.647612;2.37801rad)
  shape: bbox 20.52 x 3 x 34.05 mm, 41 faces (baked)
FEATURE [Part::Feature] Part__Feature024  label="[Fix 1] 1.Ref - Capit 1"
  Placement = pos=(-47.5526,70.75,24.0827) rot=(0.416127,0.642977,0.642977;3.93025rad)
  shape: bbox 22.68 x 3 x 63.55 mm, 36 faces (baked)
FEATURE [Part::Feature] Part__Feature025  label="[Fix 1] 1.Ref - Capit 009"
  Placement = pos=(-47.5526,73.75,24.0827) rot=(0.416127,0.642977,0.642977;3.93025rad)
  shape: bbox 22.68 x 3 x 63.55 mm, 36 faces (baked)
FEATURE [Part::Feature] Part__Feature026  label="[Fix 1] 1.Ref - Capit 010"
  Placement = pos=(-106.732,73.75,23.8304) rot=(0.73767,-0.477411,0.477411;1.87047rad)
  shape: bbox 22.68 x 3 x 63.55 mm, 36 faces (baked)
FEATURE [Part::Feature] Part__Feature042  label="4. Connector 004"
  Placement = pos=(14,89.2902,-167.955) rot=(0,1,0.000129;3.14159rad)
  shape: bbox 3 x 40.01 x 46.15 mm, 32 faces (baked)
FEATURE [Part::Feature] Part__Feature043  label="3. Link Arm 2"
  Placement = pos=(-15,177.679,-79.5669) rot=(0,0.92388,-0.382683;3.14159rad)
  shape: bbox 5 x 104.8 x 103.4 mm, 28 faces (baked)
FEATURE [Part::Feature] Part__Feature044  label="2. Link Arm Servo 1"
  Placement = pos=(-10,89.2902,8.82146) rot=(1,0,0;3.92699rad)
  shape: bbox 5 x 110.9 x 110.9 mm, 53 faces (baked)
FEATURE [Part::Feature] Part__Feature045  label="1. Arm Mount C"
  Placement = pos=(-2e-15,53.05,8.825) rot=(0,1,0;3.14159rad)
  shape: bbox 5 x 53.74 x 47.5 mm, 23 faces (baked)
FEATURE [Part::Feature] Part__Feature020  label="[Fix 1] 1.Ref - Capit 2"
  Placement = pos=(-95.7321,78.25,48.3304) rot=(0.758675,0.460658,-0.460658;1.84353rad)
  shape: bbox 21.06 x 3 x 33.84 mm, 41 faces (baked)
FEATURE [Part::Feature] Part__Feature021  label="[Fix 1] 1.Ref - Capit 006"
  Placement = pos=(-81.8942,69.25,21.7126) rot=(0.394521,-0.649751,0.649751;2.39004rad)
  shape: bbox 21.06 x 3 x 33.84 mm, 41 faces (baked)
FEATURE [Part::Feature] Part__Feature022  label="[Fix 1] 1.Ref - Capit 007"
  Placement = pos=(-71.8942,78.25,21.7126) rot=(0.751922,-0.466162,0.466162;1.85213rad)
  shape: bbox 20.52 x 3 x 34.05 mm, 41 faces (baked)
FEATURE [Part::Feature] Part__Feature046  label="1. Servo Mount B"
  Placement = pos=(-24.9,48.05,-11.175) rot=(0,1,0;3.14159rad)
  shape: bbox 5 x 72.74 x 70.43 mm, 45 faces (baked)
FEATURE [Part::Feature] Part__Feature027  label="[Fix 1] 1.Ref - Capit 011"
  Placement = pos=(-106.732,76.75,23.8304) rot=(0.73767,-0.477411,0.477411;1.87047rad)
  shape: bbox 22.68 x 3 x 63.55 mm, 36 faces (baked)
FEATURE [Part::Feature] Part__Feature028  label="[Fix 1] 1.Ref - Capit 5"
  Placement = pos=(-76.8942,76.75,-28.2874) rot=(0,1,0;1.5708rad)
  shape: bbox 19.1 x 9.5 x 9.5 mm, 21 faces (baked)
FEATURE [Part::Feature] Part__Feature029  label="[Fix 1] 1.Ref - Capit 012"
  Placement = pos=(-76.8942,73.75,-28.2874) rot=(0.707107,0,-0.707107;3.14159rad)
  shape: bbox 19.1 x 9.5 x 9.5 mm, 21 faces (baked)
FEATURE [Part::Feature] Part__Feature047  label="2. Link Arm 1"
  Placement = pos=(5,89.2867,8.825) rot=(1,0,0;3.92699rad)
  shape: bbox 5 x 108.4 x 108.4 mm, 29 faces (baked)
FEATURE [Part::Feature] Part__Feature048  label="1. Servo Mount A"
  Placement = pos=(32.9,48.05,-11.175) rot=(0,1,0;3.14159rad)
  shape: bbox 5 x 66.67 x 70.43 mm, 39 faces (baked)
FEATURE [Part::Feature] Part__Feature049  label="4. Connector 1B"
  Placement = pos=(-22,158.482,-32.8677) rot=(0,0.923873,0.382699;3.14159rad)
  shape: bbox 3 x 101.9 x 101.9 mm, 18 faces (baked)
FEATURE [Part::Feature] Part__Feature015  label="4. Connector 4"
  Placement = pos=(-2.5,98.1293,-203.103) rot=(0.000129,-1,-0.000129;1.5708rad)
  shape: bbox 37 x 60 x 5.015 mm, 38 faces (baked)
FEATURE [Part::Feature] Part__Feature016  label="Base 2"
  Placement = pos=(0,46.55,8.825) rot=(0,1,0;3.14159rad)
  shape: bbox 85 x 3 x 92 mm, 96 faces (baked)
FEATURE [Part::Feature] Part__Feature050  label="4. Connector 003"
  Placement = pos=(17,161.764,-7.08377) rot=(0,0.92388,0.382683;3.14159rad)
  shape: bbox 3 x 101.9 x 101.9 mm, 15 faces (baked)
FEATURE [Part::Feature] Part__Feature018  label="[Fix 1] 1.Ref - Capit 4"
  Placement = pos=(-92.8942,70.75,-2.78742) rot=(0.231,-0.231,-0.945134;1.62719rad)
  shape: bbox 32.93 x 3 x 44.97 mm, 63 faces (baked)
FEATURE [Part::Feature] Part__Feature019  label="[Fix 1] 1.Ref - Capit 005"
  Placement = pos=(-60.8942,67.75,-2.78742) rot=(0.222664,0.222664,0.949127;1.62298rad)
  shape: bbox 32.45 x 3 x 45.3 mm, 63 faces (baked)
FEATURE [Part::Feature] Part__Feature051  label="4. Connector 3"
  Placement = pos=(-19,89.2902,-167.955) rot=(0,1,0.000129;3.14159rad)
  shape: bbox 3 x 40.01 x 46.15 mm, 32 faces (baked)
FEATURE [Part::Feature] Part__Feature052  label="4. Connector 2"
  Placement = pos=(-19,177.679,-79.5669) rot=(0,1,0.000129;3.14159rad)
  shape: bbox 3 x 37.5 x 35 mm, 22 faces (baked)
FEATURE [Part::Feature] Part__Feature053  label="3. Link Arm Servo 2A"
  Placement = pos=(10,177.675,-79.5633) rot=(0,0.923887,-0.382665;3.14159rad)
  shape: bbox 5 x 131.7 x 131.7 mm, 34 faces (baked)
FEATURE [Part::Feature] Part__Feature017  label="[Fix 1] 1.Ref - Capit 3"
  Placement = pos=(-60.8942,73.75,-2.78742) rot=(0,0,1;0rad)
  shape: bbox 75 x 3 x 54 mm, 62 faces (baked)
FEATURE [App::Part] _Fix_1__1_Ref___ARM  label="[Fix 1] 1.Ref - ARM"
  Group = -> [Part__Feature017,Part__Feature018,Part__Feature019,Part__Feature020,Part__Feature021,Part__Feature022,Part__Feature023,Part__Feature024,Part__Feature025,Part__Feature026,Part__Feature027,Part__Feature028,Part__Feature029,Part__Feature030,Part__Feature031]
  Origin = -> Origin027
  Placement = pos=(-77.75,166.211,-251.773) rot=(0.707107,0.707107,9.1e-05;3.14177rad)
FEATURE [App::Part] Robot_Arm_V_1_1  label="Robot Arm V.1.1"
  Group = -> [Part__Feature046,Part__Feature048,Part__Feature045,Part__Feature044,Part__Feature047,Part__Feature040,Part__Feature053,Part__Feature043,Part__Feature052,Part__Feature041,Part__Feature014,Part__Feature050,Part__Feature051,Part__Feature049,Part__Feature042,Part__Feature015,Part__Feature016,_Fix_1__1_Ref___ARM,Part__Feature032,Part__Feature033,Part__Feature034,Part__Feature035,Part__Feature036,+3 more]
  Origin = -> Origin028
FEATURE [Part::FeaturePython] Clone001  label="Robot Arm V.1.003"  # WARN: FeaturePython — macro-defined, semantics opaque (R4)
  AttacherType = Attacher::AttachEngine3D
  Fuse = false
  Scale = (2,2,2)
FEATURE [App::Part] Robotarm
  Group = -> [LCS_0012,Robot_Arm_V_1_1,Clone001]
  Origin = -> Origin026
FEATURE [App::DocumentObjectGroup] Parts
  Group = -> [OCPMDC4mv2,Fan750mm,Roof,NSV,Loeschflasche,Part,AirBox,Schraubenfundament,Fan1000mm,OCPceiling,HotColdSeperator,Robotarm]
FEATURE [App::Link] Robotarm001
  AssemblyType = Asm4EE
  AttachedBy = #LCS_0012
  AttachedTo = OCPceiling002#LCS_0010
  AttachmentOffset = pos=(0,50,100) rot=(1,0,0;4.71239rad)
  LinkPlacement = pos=(0,-325,2450) rot=(1,0,0;4.71239rad)
  LinkedObject = -> Robotarm
  Placement = pos=(0,-325,2450) rot=(1,0,0;4.71239rad)
  expr: Placement = OCPceiling002.Placement * LCS_0010.Placement * AttachmentOffset * LCS_0012.Placement ^ -1
FEATURE [App::Part] Model
  Configuration = 0
  Group = -> [LCS_Origin,Constraints,Variables,OCPMDC4mv2001,OCPRack001,OCPRack001001,OCPRack001002,OCPRack001003,OCPRack001004,OCPRack001005,OCPRack001006,OCPRack001007,OCPRack001008,OCPRack001009,Roof001,NSV001,Loeschflasche001,AirBox001,Schraubenfundament001,Schraubenfundament002,Schraubenfundament003,Schraubenfundament004,Schraubenfundament005,Schraubenfundament006,Schraubenfundament007,+12 more]
  Origin = -> Origin001
  Type = Assembly4 Model
